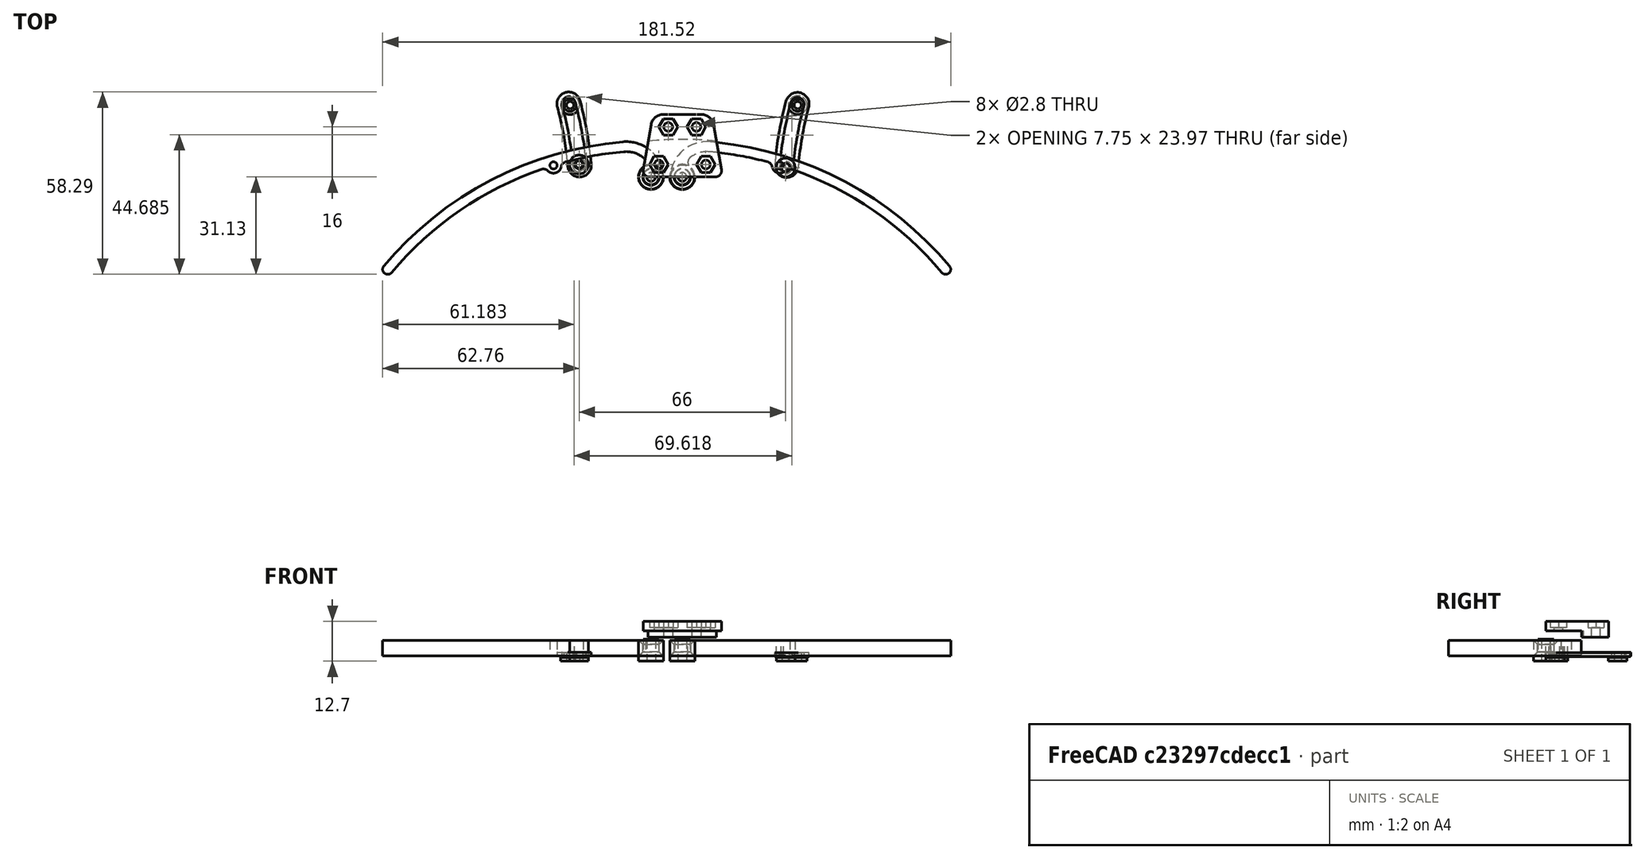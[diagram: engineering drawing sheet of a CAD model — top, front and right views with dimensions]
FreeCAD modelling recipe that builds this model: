
FCSTD DOCUMENT  (FreeCAD 0.19R24276 (Git))
Label: PB3D_TriPlate_FrontBumper
License: All rights reserved
LicenseURL: http://en.wikipedia.org/wiki/All_rights_reserved
objects: Sketcher::SketchObject×23, PartDesign::Body×13, PartDesign::Pad×7, Mesh::Feature×7, PartDesign::Revolution×6, PartDesign::Pocket×5, App::Part×5, PartDesign::Groove×2, Spreadsheet::Sheet×1, PartDesign::Plane×1
note: 77 computed .brp shape members not serialized (recipe doc carries the construction recipe); baked Part::Feature solids carry a one-line shape summary decoded from their .brp

FEATURE [Spreadsheet::Sheet] Spreadsheet  label="params"
  cells = A2=M2 Bolt Clearances; C2=M2.5 Bolt Clearances; A3=Hole Clear Diam; B3(m2_hole_clear_diam)==2.3mm; C3=Hole Clear Diam; D3(m25_hole_clear_diam)==2.8mm; E3=Std Rad; F3(std_rad)==2mm; A4=Head Clear Diam; B4(m2_head_clear_diam)==4mm; C4=Head Clear Diam; D4(m25_head_clear_diam)==5mm; A5=Head Min Depth; B5(m2_head_min_depth)==1.3mm; C5=Head Min Depth; D5(m25_head_min_depth)==1.6mm; A6=Nut Clear Flat; B6(m2_nut_clear_flat)==4.2mm; C6=Nut Clear Flat; D6(m25_nut_clear_flat)==5.2mm; A7=Nut Min Depth; B7(m2_nut_min_depth)==1.75mm; C7=Nut Min Depth; D7(m25_nut_min_depth)==2mm; A9=Bump Whisk Dims; C9=Bump Mt Plate Dims; E9=Bump Slide Dims; G9=Bumper Slide Pin; A10=Bump Diam; B10(bump_diam)==225mm; C10=MtPlate Tot Thick; D10(mtplate_tot_thick)==5mm; E10=Slide Maj Rad; F10(slide_maj_rad)==bump_diam / 2; G10=SlidePin Stop Diam; H10(slidepin_stop_diam)==6mm; A11=Bump Width; B11(bump_width)==3.2mm; C11=MtPlate Inset Thick; D11(mtplate_inset_thick)==2mm; E11=Slide Internal Width; F11(slide_internal_width)==slidepin_pin_diam + 0.3mm; G11=SlidePin Stop Height; H11(slidepin_stop_height)==1.2mm; A12=Bump Thick; B12(bump_thick)==5mm; C12=MtPlate Front Width; D12(mtplate_front_width)==20mm; E12=Slide Hoop Width; F12(slide_hoop_width)==1.6mm; G12=SlidePin Pin Diam; H12(slidepin_pin_diam)==4mm; A13=Bump Pivot Out Diam; B13(bump_pivot_out_diam)==8mm; C13=MtPlate Front Rad; D13(mtplate_front_rad)==4mm; E13=Slide Length; F13(slide_leng)==20mm; G13=SlidePin Pin Height; H13(slidepin_pin_height)==1.5mm; A14=Bump Pivot Innner Diam; B14(bump_pivot_inn_diam)==5.3mm; C14=MtPlate Back Width; D14(mtplate_back_width)==25mm; E14=Slide Thickness; F14(slide_thickness)==1.2mm; A15=Bump Slide Mt Outer Diam; B15(bump_slidemt_out_diam)==5mm; C15=MtPlate Length; D15(mtplate_leng)==20mm; G15=PinOffset Diam; H15(pinoffset_diam)==slidepin_stop_diam; A16=Bump Pivot Offset; B16(bump_pivot_offset)==8mm; C16=MtPlate Piv Hole Width; D16(mtplate_piv_hole_width)==9mm; G16=PinOffset Height; H16(pinoffset_height)==bump_thick; C17=MtPlate Hole Space L; D17(mtplate_hole_space_leng)==12mm; A18=Bump Pivot Height Tol; B18(bump_pivot_height_tol)==0.3mm; C18=MtPlate Mt Hole Width; D18(mtplate_mt_hole_width)==15mm; A19=Bump Pivot Plate Thick; B19(bump_pivot_plate_thick)==1.6mm; C19=MtPlate Mt Hole Offset L; D19(mtplate_mt_hole_offset_leng)==4mm; C20=MtPlate Circ Inset Offset ; D20(mtplate_circ_inset_offset)==12mm; A21=Bump Sweep Ang; B21(bump_sweep_ang)=45; A22=Bump Piv Angle; B22(bump_piv_ang)=12; A24=Bump Pivot Tol; B24(bump_pivot_tol)==0.3mm
FEATURE [Sketcher::SketchObject] Sketch  label="Sketch_Main_Ext"
  FullyConstrained = true
  MapMode = 5
  Support = -> [XY_Plane003]
  expr: Constraints[44] = <<params>>.bump_piv_ang
  expr: Constraints[16] = <<params>>.bump_diam
  expr: Constraints[27] = <<params>>.bump_diam
  expr: Constraints[55] = <<params>>.std_rad
  expr: Constraints[43] = 90 - <<params>>.bump_sweep_ang
  expr: Constraints[18] = <<params>>.bump_width
  expr: Constraints[35] = <<params>>.bump_slidemt_out_diam
  expr: Constraints[13] = <<params>>.bump_pivot_offset
  expr: Constraints[15] = <<params>>.bump_pivot_out_diam
  expr: Constraints[53] = <<params>>.std_rad
  sketch-geometry (21):
    g0: ArcOfCircle CenterX=0 CenterY=0 CenterZ=0 NormalX=0 NormalY=0 NormalZ=1 AngleXU=0 Radius=4 StartAngle=3.14159 EndAngle=6.28319
    g1: LineSegment StartX=8 StartY=-100.5 StartZ=0 EndX=117.3 EndY=-100.5 EndZ=0
    g2: LineSegment StartX=8 StartY=8.80001 StartZ=0 EndX=8 EndY=12 EndZ=0
    g3: ArcOfCircle CenterX=8 CenterY=-100.5 CenterZ=0 NormalX=0 NormalY=0 NormalZ=1 AngleXU=0 Radius=109.3 StartAngle=1.39858 EndAngle=1.5708
    g4: ArcOfCircle CenterX=8 CenterY=-100.5 CenterZ=0 NormalX=0 NormalY=0 NormalZ=1 AngleXU=0 Radius=112.5 StartAngle=0.785398 EndAngle=1.5708
    g5: LineSegment StartX=8 StartY=8.80001 StartZ=0 EndX=8 EndY=0 EndZ=0
    g6: LineSegment StartX=8 StartY=-100.5 StartZ=0 EndX=8 EndY=0 EndZ=0
    g7: ArcOfCircle CenterX=8 CenterY=-100.5 CenterZ=0 NormalX=0 NormalY=0 NormalZ=1 AngleXU=0 Radius=109.3 StartAngle=0.785398 EndAngle=1.32413
    g8: LineSegment StartX=8 StartY=-100.5 StartZ=0 EndX=30.7247 EndY=6.41154 EndZ=0
    g9: LineSegment StartX=8 StartY=-100.5 StartZ=0 EndX=85.2868 EndY=-23.2132 EndZ=0
    g10: LineSegment StartX=85.2868 StartY=-23.2132 StartZ=0 EndX=87.5495 EndY=-20.9505 EndZ=0
    g11: Circle CenterX=8 CenterY=-100.5 CenterZ=0 NormalX=0 NormalY=0 NormalZ=1 AngleXU=0 Radius=112.5
    g12: Circle CenterX=8 CenterY=-100.5 CenterZ=0 NormalX=0 NormalY=0 NormalZ=1 AngleXU=0 Radius=109.3
    g13: ArcOfCircle CenterX=30.7247 CenterY=6.41154 CenterZ=0 NormalX=0 NormalY=0 NormalZ=1 AngleXU=0 Radius=2.5 StartAngle=3.41123 EndAngle=5.59466
    g14: ArcOfCircle CenterX=86.4181 CenterY=-22.0819 CenterZ=0 NormalX=0 NormalY=0 NormalZ=1 AngleXU=0 Radius=1.6 StartAngle=3.92699 EndAngle=7.06858
    g15: ArcOfCircle CenterX=8.00001 CenterY=1.03132e-07 CenterZ=0 NormalX=0 NormalY=0 NormalZ=1 AngleXU=0 Radius=12 StartAngle=1.5708 EndAngle=3.14159
    g16: ArcOfCircle CenterX=0 CenterY=0 CenterZ=0 NormalX=0 NormalY=0 NormalZ=1 AngleXU=0 Radius=4 StartAngle=0 EndAngle=0.976411
    g17: ArcOfCircle CenterX=8.00001 CenterY=1.03132e-07 CenterZ=0 NormalX=0 NormalY=0 NormalZ=1 AngleXU=0 Radius=8.80001 StartAngle=1.5708 EndAngle=2.32177
    g18: ArcOfCircle CenterX=3.36 CenterY=4.97096 CenterZ=0 NormalX=0 NormalY=0 NormalZ=1 AngleXU=0 Radius=2 StartAngle=2.32177 EndAngle=4.118
    g19: ArcOfCircle CenterX=26.3873 CenterY=5.2128 CenterZ=0 NormalX=0 NormalY=0 NormalZ=1 AngleXU=0 Radius=2 StartAngle=0.269641 EndAngle=1.39858
    g20: ArcOfCircle CenterX=34.1996 CenterY=3.55226 CenterZ=0 NormalX=0 NormalY=0 NormalZ=1 AngleXU=0 Radius=2 StartAngle=1.32413 EndAngle=2.45307
  constraints (57):
    c: Coincident(g0,g-1)
    c: PointOnObject(g0,g-1)
    c: PointOnObject(g0,g-1)
    c: Horizontal(g1)
    c: Vertical(g2)
    c: Coincident(g4,g3)
    c: Coincident(g4,g2)
    c: Coincident(g5,g3)
    c: PointOnObject(g5,g-1)
    c: Vertical(g5)
    c: Coincident(g6,g3)
    c: Coincident(g6,g5)
    c: Vertical(g6)
    c: DistanceX(g0,g5) = 8
    c: Coincident(g2,g3)
    c: Diameter(g0) = 8
    c: Diameter(g4) = 225
    c: Coincident(g1,g3)
    c: DistanceY(g3,g4) = 3.2
    c: Coincident(g7,g3)
    c: Coincident(g8,g3)
    c: Coincident(g9,g3)
    c: Coincident(g9,g7)
    c: Coincident(g10,g7)
    c: Coincident(g10,g4)
    c: Parallel(g9,g10)
    c: Coincident(g11,g3)
    c: Diameter(g11) = 225
    c: Coincident(g12,g3)
    c: PointOnObject(g3,g12)
    c: PointOnObject(g13,g12)
    c: Coincident(g8,g13)
    c: PointOnObject(g14,g10)
    c: Coincident(g14,g7)
    c: Coincident(g14,g4)
    c: Diameter(g13) = 5
    c: Coincident(g15,g4)
    c: Coincident(g15,g0)
    c: Coincident(g16,g0)
    c: Coincident(g17,g15)
    c: Coincident(g17,g3)
    c: Coincident(g16,g0)
    c: PointOnObject(g1,g12)
    c: Angle(g1,g9) = 0.785398
    c: Angle(g8,g6) = 0.20944
    c: Tangent(g0,g15)
    c: Tangent(g15,g4)
    c: Tangent(g16,g18) = 1.5708
    c: Tangent(g17,g18) = -1.5708
    c: Tangent(g13,g19) = 1.5708
    c: Tangent(g3,g19) = -1.5708
    c: Tangent(g13,g20) = 1.5708
    c: Tangent(g7,g20) = -1.5708
    c: Radius(g18) = 2
    c: Equal(g19,g20)
    c: Radius(g20) = 2
    c: PointOnObject(g7,g12)
FEATURE [PartDesign::Pad] Pad  label="MainExt"
  Direction = (1,1,1)
  Length = 5
  Length2 = 100
  Profile = -> Sketch
  Reversed = true
  Type = 0
  expr: Length = <<params>>.bump_thick
FEATURE [Sketcher::SketchObject] Sketch001  label="Sketch_Main_Ext_Temp"
  FullyConstrained = true
  MapMode = 5
  Support = -> [XY_Plane003]
  expr: Constraints[53] = <<params>>.std_rad
  expr: Constraints[15] = <<params>>.bump_pivot_out_diam
  expr: Constraints[13] = <<params>>.bump_pivot_offset
  expr: Constraints[35] = <<params>>.bump_slidemt_out_diam
  expr: Constraints[18] = <<params>>.bump_width
  expr: Constraints[55] = <<params>>.std_rad
  expr: Constraints[27] = <<params>>.bump_diam
  expr: Constraints[16] = <<params>>.bump_diam
  sketch-geometry (21):
    g0: ArcOfCircle CenterX=0 CenterY=0 CenterZ=0 NormalX=0 NormalY=0 NormalZ=1 AngleXU=0 Radius=4 StartAngle=3.14159 EndAngle=6.28319
    g1: LineSegment StartX=8 StartY=-100.5 StartZ=0 EndX=117.3 EndY=-100.5 EndZ=0
    g2: LineSegment StartX=8 StartY=8.79997 StartZ=0 EndX=8 EndY=12 EndZ=0
    g3: ArcOfCircle CenterX=8 CenterY=-100.5 CenterZ=0 NormalX=0 NormalY=0 NormalZ=1 AngleXU=0 Radius=109.3 StartAngle=1.34622 EndAngle=1.5708
    g4: ArcOfCircle CenterX=8 CenterY=-100.5 CenterZ=0 NormalX=0 NormalY=0 NormalZ=1 AngleXU=0 Radius=112.5 StartAngle=0.349066 EndAngle=1.5708
    g5: LineSegment StartX=8 StartY=8.79997 StartZ=0 EndX=8 EndY=0 EndZ=0
    g6: LineSegment StartX=8 StartY=-100.5 StartZ=0 EndX=8 EndY=0 EndZ=0
    g7: ArcOfCircle CenterX=8 CenterY=-100.5 CenterZ=0 NormalX=0 NormalY=0 NormalZ=1 AngleXU=0 Radius=109.3 StartAngle=0.349066 EndAngle=1.27177
    g8: LineSegment StartX=8 StartY=-100.5 StartZ=0 EndX=36.2889 EndY=5.07567 EndZ=0
    g9: LineSegment StartX=8 StartY=-100.5 StartZ=0 EndX=110.708 EndY=-63.1172 EndZ=0
    g10: LineSegment StartX=110.708 StartY=-63.1172 StartZ=0 EndX=113.715 EndY=-62.0228 EndZ=0
    g11: Circle CenterX=8 CenterY=-100.5 CenterZ=0 NormalX=0 NormalY=0 NormalZ=1 AngleXU=0 Radius=112.5
    g12: Circle CenterX=8 CenterY=-100.5 CenterZ=0 NormalX=0 NormalY=0 NormalZ=1 AngleXU=0 Radius=109.3
    g13: ArcOfCircle CenterX=36.2889 CenterY=5.07567 CenterZ=0 NormalX=0 NormalY=0 NormalZ=1 AngleXU=0 Radius=2.5 StartAngle=3.35887 EndAngle=5.54231
    g14: ArcOfCircle CenterX=112.212 CenterY=-62.57 CenterZ=0 NormalX=0 NormalY=0 NormalZ=1 AngleXU=0 Radius=1.6 StartAngle=3.49066 EndAngle=6.63225
    g15: ArcOfCircle CenterX=7.99997 CenterY=1.02572e-07 CenterZ=0 NormalX=0 NormalY=0 NormalZ=1 AngleXU=0 Radius=12 StartAngle=1.57079 EndAngle=3.14159
    g16: ArcOfCircle CenterX=0 CenterY=0 CenterZ=0 NormalX=0 NormalY=0 NormalZ=1 AngleXU=0 Radius=4 StartAngle=0 EndAngle=0.976409
    g17: ArcOfCircle CenterX=7.99997 CenterY=1.02572e-07 CenterZ=0 NormalX=0 NormalY=0 NormalZ=1 AngleXU=0 Radius=8.79997 StartAngle=1.57079 EndAngle=2.32177
    g18: ArcOfCircle CenterX=3.36001 CenterY=4.97095 CenterZ=0 NormalX=0 NormalY=0 NormalZ=1 AngleXU=0 Radius=2 StartAngle=2.32177 EndAngle=4.118
    g19: ArcOfCircle CenterX=31.8947 CenterY=4.10558 CenterZ=0 NormalX=0 NormalY=0 NormalZ=1 AngleXU=0 Radius=2 StartAngle=0.217281 EndAngle=1.34622
    g20: ArcOfCircle CenterX=39.6094 CenterY=2.03845 CenterZ=0 NormalX=0 NormalY=0 NormalZ=1 AngleXU=0 Radius=2 StartAngle=1.27177 EndAngle=2.40071
  constraints (57):
    c: Coincident(g0,g-1)
    c: PointOnObject(g0,g-1)
    c: PointOnObject(g0,g-1)
    c: Horizontal(g1)
    c: Vertical(g2)
    c: Coincident(g4,g3)
    c: Coincident(g4,g2)
    c: Coincident(g5,g3)
    c: PointOnObject(g5,g-1)
    c: Vertical(g5)
    c: Coincident(g6,g3)
    c: Coincident(g6,g5)
    c: Vertical(g6)
    c: DistanceX(g0,g5) = 8
    c: Coincident(g2,g3)
    c: Diameter(g0) = 8
    c: Diameter(g4) = 225
    c: Coincident(g1,g3)
    c: DistanceY(g3,g4) = 3.2
    c: Coincident(g7,g3)
    c: Coincident(g8,g3)
    c: Coincident(g9,g3)
    c: Coincident(g9,g7)
    c: Coincident(g10,g7)
    c: Coincident(g10,g4)
    c: Parallel(g9,g10)
    c: Coincident(g11,g3)
    c: Diameter(g11) = 225
    c: Coincident(g12,g3)
    c: PointOnObject(g3,g12)
    c: PointOnObject(g13,g12)
    c: Coincident(g8,g13)
    c: PointOnObject(g14,g10)
    c: Coincident(g14,g7)
    c: Coincident(g14,g4)
    c: Diameter(g13) = 5
    c: Coincident(g15,g4)
    c: Coincident(g15,g0)
    c: Coincident(g16,g0)
    c: Coincident(g17,g15)
    c: Coincident(g17,g3)
    c: Coincident(g16,g0)
    c: PointOnObject(g1,g12)
    c: Angle(g1,g9) = 0.349066
    c: Angle(g8,g6) = 0.261799
    c: Tangent(g0,g15)
    c: Tangent(g15,g4)
    c: Tangent(g16,g18) = 1.5708
    c: Tangent(g17,g18) = -1.5708
    c: Tangent(g13,g19) = 1.5708
    c: Tangent(g3,g19) = -1.5708
    c: Tangent(g13,g20) = 1.5708
    c: Tangent(g7,g20) = -1.5708
    c: Radius(g18) = 2
    c: Equal(g19,g20)
    c: Radius(g20) = 2
    c: PointOnObject(g7,g12)
FEATURE [Sketcher::SketchObject] Sketch002  label="Sketch_SlideHole"
  FullyConstrained = true
  MapMode = 5
  Support = -> [XY_Plane003]
  expr: Constraints[44] = <<params>>.bump_piv_ang
  expr: Constraints[16] = <<params>>.bump_diam
  expr: Constraints[27] = <<params>>.bump_diam
  expr: Constraints[55] = <<params>>.std_rad
  expr: Constraints[18] = <<params>>.bump_width
  expr: Constraints[35] = <<params>>.bump_slidemt_out_diam
  expr: Constraints[13] = <<params>>.bump_pivot_offset
  expr: Constraints[53] = <<params>>.std_rad
  expr: Constraints[15] = <<params>>.bump_pivot_out_diam
  expr: Constraints[58] = <<params>>.m2_hole_clear_diam
  sketch-geometry (22):
    g0: ArcOfCircle CenterX=0 CenterY=0 CenterZ=0 NormalX=0 NormalY=0 NormalZ=1 AngleXU=0 Radius=4 StartAngle=3.14159 EndAngle=6.28319
    g1: LineSegment StartX=8 StartY=-100.5 StartZ=0 EndX=117.3 EndY=-100.5 EndZ=0
    g2: LineSegment StartX=8 StartY=8.8 StartZ=0 EndX=8 EndY=12 EndZ=0
    g3: ArcOfCircle CenterX=8 CenterY=-100.5 CenterZ=0 NormalX=0 NormalY=0 NormalZ=1 AngleXU=0 Radius=109.3 StartAngle=1.39858 EndAngle=1.5708
    g4: ArcOfCircle CenterX=8 CenterY=-100.5 CenterZ=0 NormalX=0 NormalY=0 NormalZ=1 AngleXU=0 Radius=112.5 StartAngle=0.349066 EndAngle=1.5708
    g5: LineSegment StartX=8 StartY=8.8 StartZ=0 EndX=8 EndY=0 EndZ=0
    g6: LineSegment StartX=8 StartY=-100.5 StartZ=0 EndX=8 EndY=0 EndZ=0
    g7: ArcOfCircle CenterX=8 CenterY=-100.5 CenterZ=0 NormalX=0 NormalY=0 NormalZ=1 AngleXU=0 Radius=109.3 StartAngle=0.349066 EndAngle=1.32413
    g8: LineSegment StartX=8 StartY=-100.5 StartZ=0 EndX=30.7247 EndY=6.41154 EndZ=0
    g9: LineSegment StartX=8 StartY=-100.5 StartZ=0 EndX=110.708 EndY=-63.1172 EndZ=0
    g10: LineSegment StartX=110.708 StartY=-63.1172 StartZ=0 EndX=113.715 EndY=-62.0227 EndZ=0
    g11: Circle CenterX=8 CenterY=-100.5 CenterZ=0 NormalX=0 NormalY=0 NormalZ=1 AngleXU=0 Radius=112.5
    g12: Circle CenterX=8 CenterY=-100.5 CenterZ=0 NormalX=0 NormalY=0 NormalZ=1 AngleXU=0 Radius=109.3
    g13: ArcOfCircle CenterX=30.7247 CenterY=6.41154 CenterZ=0 NormalX=0 NormalY=0 NormalZ=1 AngleXU=0 Radius=2.5 StartAngle=3.41123 EndAngle=5.59466
    g14: ArcOfCircle CenterX=112.212 CenterY=-62.57 CenterZ=0 NormalX=0 NormalY=0 NormalZ=1 AngleXU=0 Radius=1.6 StartAngle=3.49066 EndAngle=6.63225
    g15: ArcOfCircle CenterX=8 CenterY=3.30857e-07 CenterZ=0 NormalX=0 NormalY=0 NormalZ=1 AngleXU=0 Radius=12 StartAngle=1.5708 EndAngle=3.14159
    g16: ArcOfCircle CenterX=0 CenterY=0 CenterZ=0 NormalX=0 NormalY=0 NormalZ=1 AngleXU=0 Radius=4 StartAngle=0 EndAngle=0.976411
    g17: ArcOfCircle CenterX=8 CenterY=3.30857e-07 CenterZ=0 NormalX=0 NormalY=0 NormalZ=1 AngleXU=0 Radius=8.8 StartAngle=1.5708 EndAngle=2.32177
    g18: ArcOfCircle CenterX=3.36 CenterY=4.97096 CenterZ=0 NormalX=0 NormalY=0 NormalZ=1 AngleXU=0 Radius=2 StartAngle=2.32177 EndAngle=4.118
    g19: ArcOfCircle CenterX=26.3873 CenterY=5.2128 CenterZ=0 NormalX=0 NormalY=0 NormalZ=1 AngleXU=0 Radius=2 StartAngle=0.269641 EndAngle=1.39858
    g20: ArcOfCircle CenterX=34.1996 CenterY=3.55226 CenterZ=0 NormalX=0 NormalY=0 NormalZ=1 AngleXU=0 Radius=2 StartAngle=1.32413 EndAngle=2.45307
    g21: Circle CenterX=30.7247 CenterY=6.41154 CenterZ=0 NormalX=0 NormalY=0 NormalZ=1 AngleXU=0 Radius=1.15
  constraints (59):
    c: Coincident(g0,g-1)
    c: PointOnObject(g0,g-1)
    c: PointOnObject(g0,g-1)
    c: Horizontal(g1)
    c: Vertical(g2)
    c: Coincident(g4,g3)
    c: Coincident(g4,g2)
    c: Coincident(g5,g3)
    c: PointOnObject(g5,g-1)
    c: Vertical(g5)
    c: Coincident(g6,g3)
    c: Coincident(g6,g5)
    c: Vertical(g6)
    c: DistanceX(g0,g5) = 8
    c: Coincident(g2,g3)
    c: Diameter(g0) = 8
    c: Diameter(g4) = 225
    c: Coincident(g1,g3)
    c: DistanceY(g3,g4) = 3.2
    c: Coincident(g7,g3)
    c: Coincident(g8,g3)
    c: Coincident(g9,g3)
    c: Coincident(g9,g7)
    c: Coincident(g10,g7)
    c: Coincident(g10,g4)
    c: Parallel(g9,g10)
    c: Coincident(g11,g3)
    c: Diameter(g11) = 225
    c: Coincident(g12,g3)
    c: PointOnObject(g3,g12)
    c: PointOnObject(g13,g12)
    c: Coincident(g8,g13)
    c: PointOnObject(g14,g10)
    c: Coincident(g14,g7)
    c: Coincident(g14,g4)
    c: Diameter(g13) = 5
    c: Coincident(g15,g4)
    c: Coincident(g15,g0)
    c: Coincident(g16,g0)
    c: Coincident(g17,g15)
    c: Coincident(g17,g3)
    c: Coincident(g16,g0)
    c: PointOnObject(g1,g12)
    c: Angle(g1,g9) = 0.349066
    c: Angle(g8,g6) = 0.20944
    c: Tangent(g0,g15)
    c: Tangent(g15,g4)
    c: Tangent(g16,g18) = 1.5708
    c: Tangent(g17,g18) = -1.5708
    c: Tangent(g13,g19) = 1.5708
    c: Tangent(g3,g19) = -1.5708
    c: Tangent(g13,g20) = 1.5708
    c: Tangent(g7,g20) = -1.5708
    c: Radius(g18) = 2
    c: Equal(g19,g20)
    c: Radius(g20) = 2
    c: PointOnObject(g7,g12)
    c: Coincident(g21,g8)
    c: Diameter(g21) = 2.3
FEATURE [PartDesign::Pocket] Pocket  label="SlideMtHole"
  BaseFeature = -> Pad
  Length = 5
  Length2 = 100
  Midplane = true
  Profile = -> Sketch002
  Type = 1
FEATURE [Sketcher::SketchObject] Sketch003
  FullyConstrained = true
  MapMode = 5
  Placement = pos=(0,0,0) rot=(1,0,0;1.5708rad)
  Support = -> [XZ_Plane003]
  expr: Constraints[16] = <<params>>.bump_pivot_inn_diam / 2
  expr: Constraints[17] = <<params>>.bump_thick
  expr: Constraints[18] = <<params>>.bump_thick / 4
  sketch-geometry (7):
    g0: LineSegment StartX=0 StartY=0 StartZ=0 EndX=3.9 EndY=0 EndZ=0
    g1: LineSegment StartX=3.9 StartY=0 StartZ=0 EndX=2.65 EndY=-1.25 EndZ=0
    g2: LineSegment StartX=2.65 StartY=-1.25 StartZ=0 EndX=2.65 EndY=-3.75 EndZ=0
    g3: LineSegment StartX=2.65 StartY=-3.75 StartZ=0 EndX=3.9 EndY=-5 EndZ=0
    g4: LineSegment StartX=3.9 StartY=-5 StartZ=0 EndX=0 EndY=-5 EndZ=0
    g5: LineSegment StartX=0 StartY=-5 StartZ=0 EndX=0 EndY=0 EndZ=0
    g6: LineSegment StartX=3.9 StartY=0 StartZ=0 EndX=3.9 EndY=-5 EndZ=0
  constraints (19):
    c: Coincident(g0,g-1)
    c: PointOnObject(g0,g-1)
    c: Coincident(g1,g0)
    c: Coincident(g2,g1)
    c: Vertical(g2)
    c: Coincident(g3,g2)
    c: Coincident(g4,g3)
    c: PointOnObject(g4,g-2)
    c: Coincident(g5,g4)
    c: Coincident(g5,g0)
    c: Horizontal(g4)
    c: Coincident(g6,g0)
    c: Coincident(g6,g3)
    c: Vertical(g6)
    c: Angle(g0,g1) = 0.785398
    c: Angle(g3,g4) = 0.785398
    c: DistanceX(g4,g2) = 2.65
    c: DistanceY(g4,g0) = 5
    c: DistanceY(g1,g0) = 1.25
FEATURE [PartDesign::Groove] Groove
  Angle = 360
  Axis = (0,-2e-16,1)
  Base = (0,0,0)
  BaseFeature = -> Pocket
  Profile = -> Sketch003
  ReferenceAxis = -> Sketch003 [V_Axis]
FEATURE [PartDesign::Body] Body001  label="BumpWhisker"
  Group = -> [Sketch,Pad,Sketch001,Sketch002,Pocket,Sketch003,Groove]
  Origin = -> Origin003
  Placement = pos=(0,0,-6) rot=(0,0,-1;0.087266rad)
  Tip = -> Groove
FEATURE [Sketcher::SketchObject] Sketch004
  FullyConstrained = true
  MapMode = 5
  Placement = pos=(0,0,0) rot=(1,0,0;1.5708rad)
  Support = -> [XZ_Plane010]
  expr: Constraints[15] = <<params>>.bump_thick / 4
  expr: Constraints[20] = <<params>>.bump_pivot_out_diam / 2
  expr: Constraints[16] = <<params>>.bump_thick
  expr: Constraints[13] = <<params>>.bump_pivot_plate_thick
  expr: Constraints[14] = <<params>>.bump_pivot_height_tol
  expr: Constraints[22] = <<params>>.m25_hole_clear_diam / 2
  expr: Constraints[21] = (<<params>>.bump_pivot_inn_diam - <<params>>.bump_pivot_tol) / 2
  sketch-geometry (8):
    g0: LineSegment StartX=1.4 StartY=0.3 StartZ=0 EndX=2.5 EndY=0.3 EndZ=0
    g1: LineSegment StartX=2.5 StartY=0.3 StartZ=0 EndX=2.5 EndY=-3.75 EndZ=0
    g2: LineSegment StartX=2.5 StartY=-3.75 StartZ=0 EndX=3.75 EndY=-5 EndZ=0
    g3: LineSegment StartX=3.75 StartY=-5 StartZ=0 EndX=4 EndY=-5 EndZ=0
    g4: LineSegment StartX=4 StartY=-5 StartZ=0 EndX=4 EndY=-6.6 EndZ=0
    g5: LineSegment StartX=4 StartY=-6.6 StartZ=0 EndX=1.4 EndY=-6.6 EndZ=0
    g6: LineSegment StartX=3.75 StartY=-5 StartZ=0 EndX=0 EndY=-5 EndZ=0
    g7: LineSegment StartX=1.4 StartY=0.3 StartZ=0 EndX=1.4 EndY=-6.6 EndZ=0
  constraints (24):
    c: Horizontal(g0)
    c: Coincident(g1,g0)
    c: Vertical(g1)
    c: Coincident(g2,g1)
    c: Coincident(g3,g2)
    c: Horizontal(g3)
    c: Coincident(g4,g3)
    c: Vertical(g4)
    c: Coincident(g5,g4)
    c: Horizontal(g5)
    c: Coincident(g6,g2)
    c: Horizontal(g6)
    c: Angle(g2,g6) = 0.785398
    c: DistanceY(g4,g3) = 1.6
    c: DistanceY(g-1,g0) = 0.3
    c: DistanceY(g2,g1) = 1.25
    c: DistanceY(g2,g-1) = 5
    c: Coincident(g7,g0)
    c: Coincident(g7,g5)
    c: Vertical(g7)
    c: DistanceX(g-1,g4) = 4
    c: DistanceX(g-1,g0) = 2.5
    c: DistanceX(g-1,g0) = 1.4
    c: PointOnObject(g6,g-2)
FEATURE [PartDesign::Revolution] Revolution
  Angle = 360
  Axis = (0,-2e-16,1)
  Base = (0,0,0)
  Placement = pos=(0,0,0) rot=(1,0,0;1.5708rad)
  Profile = -> Sketch004
  ReferenceAxis = -> Sketch004 [V_Axis]
  Reversed = true
FEATURE [PartDesign::Body] Body005  label="BumpPivot"
  Group = -> [Sketch004,Revolution]
  Origin = -> Origin010
  Placement = pos=(0,0,-6) rot=(0,0,1;0rad)
  Tip = -> Revolution
FEATURE [Sketcher::SketchObject] Sketch005  label="Sketch_MainPlate"
  FullyConstrained = true
  MapMode = 5
  Support = -> [XY_Plane001]
  expr: Constraints[20] = <<params>>.mtplate_leng
  expr: Constraints[18] = <<params>>.mtplate_front_width
  expr: Constraints[21] = <<params>>.bump_pivot_out_diam / 2
  expr: Constraints[19] = <<params>>.mtplate_back_width
  expr: Constraints[23] = <<params>>.std_rad
  sketch-geometry (10):
    g0: LineSegment StartX=-10.5297 StartY=0 StartZ=0 EndX=10.5297 EndY=0 EndZ=0
    g1: LineSegment StartX=-12.5 StartY=2.34341 StartZ=0 EndX=-10 EndY=16.6868 EndZ=0
    g2: LineSegment StartX=-6.05941 StartY=20 StartZ=0 EndX=6.05941 EndY=20 EndZ=0
    g3: LineSegment StartX=10 StartY=16.6868 StartZ=0 EndX=12.5 EndY=2.34341 EndZ=0
    g4: LineSegment StartX=0 StartY=0 StartZ=0 EndX=0 EndY=20 EndZ=0
    g5: LineSegment StartX=0 StartY=0 StartZ=0 EndX=2e-16 EndY=0 EndZ=0
    g6: ArcOfCircle CenterX=-6.05941 CenterY=16 CenterZ=0 NormalX=0 NormalY=0 NormalZ=1 AngleXU=0 Radius=4 StartAngle=1.5708 EndAngle=2.96903
    g7: ArcOfCircle CenterX=6.05941 CenterY=16 CenterZ=0 NormalX=0 NormalY=0 NormalZ=1 AngleXU=0 Radius=4 StartAngle=0.172563 EndAngle=1.5708
    g8: ArcOfCircle CenterX=-10.5297 CenterY=2 CenterZ=0 NormalX=0 NormalY=0 NormalZ=1 AngleXU=0 Radius=2 StartAngle=2.96903 EndAngle=4.71239
    g9: ArcOfCircle CenterX=10.5297 CenterY=2 CenterZ=0 NormalX=0 NormalY=0 NormalZ=1 AngleXU=0 Radius=2 StartAngle=4.71239 EndAngle=6.45575
  constraints (24):
    c: Horizontal(g0)
    c: Horizontal(g2)
    c: Coincident(g4,g-1)
    c: PointOnObject(g4,g-2)
    c: Coincident(g5,g-1)
    c: PointOnObject(g5,g-2)
    c: Tangent(g1,g6) = 1.5708
    c: Tangent(g2,g6) = 1.5708
    c: Tangent(g2,g7) = 1.5708
    c: Tangent(g3,g7) = 1.5708
    c: Tangent(g1,g8) = 1.5708
    c: Tangent(g0,g8) = -1.5708
    c: Tangent(g0,g9) = -1.5708
    c: Tangent(g3,g9) = 1.5708
    c: Equal(g9,g8)
    c: Equal(g6,g7)
    c: Symmetric(g2,g2,g4)
    c: Symmetric(g0,g0,g5)
    c: DistanceX(g1,g3) = 20
    c: DistanceX(g1,g3) = 25
    c: DistanceY(g0,g2) = 20
    c: Radius(g7) = 4
    c: PointOnObject(g0,g-1)
    c: Radius(g9) = 2
FEATURE [PartDesign::Pad] Pad001  label="MainPlateExt"
  Direction = (1,1,1)
  Length = 5
  Length2 = 100
  Profile = -> Sketch005
  Reversed = true
  Type = 0
  expr: Length = <<params>>.mtplate_tot_thick
FEATURE [PartDesign::Plane] DatumPlane  label="Datum_InsetLocZ"
  AttachmentOffset = pos=(0,0,-3) rot=(0,0,1;0rad)
  Length = 60
  MapMode = 5
  Placement = pos=(0,0,-3) rot=(0,0,1;0rad)
  ResizeMode = 0
  Support = -> [XY_Plane001]
  Width = 60
  expr: .AttachmentOffset.Base.z = -1 * (<<params>>.mtplate_tot_thick - <<params>>.mtplate_inset_thick)
FEATURE [Sketcher::SketchObject] Sketch006  label="Sketch_PivNMtHoles_Temp"
  FullyConstrained = true
  MapMode = 5
  Support = -> [XY_Plane001]
  expr: Constraints[11] = <<params>>.mtplate_piv_hole_width
  expr: Constraints[10] = <<params>>.mtplate_mt_hole_width
  expr: Constraints[9] = <<params>>.mtplate_hole_space_leng
  expr: Constraints[8] = <<params>>.mtplate_mt_hole_offset_leng
  sketch-geometry (4):
    g0: LineSegment StartX=-7.5 StartY=4 StartZ=0 EndX=7.5 EndY=4 EndZ=0
    g1: LineSegment StartX=0 StartY=0 StartZ=0 EndX=0 EndY=4 EndZ=0
    g2: LineSegment StartX=0 StartY=0 StartZ=0 EndX=0 EndY=16 EndZ=0
    g3: LineSegment StartX=-4.5 StartY=16 StartZ=0 EndX=4.5 EndY=16 EndZ=0
  constraints (12):
    c: Horizontal(g0)
    c: Coincident(g1,g-1)
    c: PointOnObject(g1,g-2)
    c: Coincident(g2,g-1)
    c: PointOnObject(g2,g-2)
    c: Horizontal(g3)
    c: Symmetric(g3,g3,g2)
    c: Symmetric(g0,g0,g1)
    c: DistanceY(g-1,g1) = 4
    c: DistanceY(g1,g2) = 12
    c: DistanceX(g0,g0) = 15
    c: DistanceX(g3,g3) = 9
FEATURE [Sketcher::SketchObject] Sketch007  label="Sketch_PivNMtHoles"
  FullyConstrained = true
  MapMode = 5
  Support = -> [XY_Plane001]
  expr: Constraints[19] = <<params>>.m25_hole_clear_diam
  expr: Constraints[8] = <<params>>.mtplate_mt_hole_offset_leng
  expr: Constraints[9] = <<params>>.mtplate_hole_space_leng
  expr: Constraints[10] = <<params>>.mtplate_mt_hole_width
  expr: Constraints[11] = <<params>>.mtplate_piv_hole_width
  sketch-geometry (8):
    g0: LineSegment StartX=-7.5 StartY=4 StartZ=0 EndX=7.5 EndY=4 EndZ=0
    g1: LineSegment StartX=0 StartY=0 StartZ=0 EndX=0 EndY=4 EndZ=0
    g2: LineSegment StartX=0 StartY=0 StartZ=0 EndX=0 EndY=16 EndZ=0
    g3: LineSegment StartX=-4.5 StartY=16 StartZ=0 EndX=4.5 EndY=16 EndZ=0
    g4: Circle CenterX=-4.5 CenterY=16 CenterZ=0 NormalX=0 NormalY=0 NormalZ=1 AngleXU=0 Radius=1.4
    g5: Circle CenterX=4.5 CenterY=16 CenterZ=0 NormalX=0 NormalY=0 NormalZ=1 AngleXU=0 Radius=1.4
    g6: Circle CenterX=7.5 CenterY=4 CenterZ=0 NormalX=0 NormalY=0 NormalZ=1 AngleXU=0 Radius=1.4
    g7: Circle CenterX=-7.5 CenterY=4 CenterZ=0 NormalX=0 NormalY=0 NormalZ=1 AngleXU=0 Radius=1.4
  constraints (20):
    c: Horizontal(g0)
    c: Coincident(g1,g-1)
    c: PointOnObject(g1,g-2)
    c: Coincident(g2,g-1)
    c: PointOnObject(g2,g-2)
    c: Horizontal(g3)
    c: Symmetric(g3,g3,g2)
    c: Symmetric(g0,g0,g1)
    c: DistanceY(g-1,g1) = 4
    c: DistanceY(g1,g2) = 12
    c: DistanceX(g0,g0) = 15
    c: DistanceX(g3,g3) = 9
    c: Coincident(g4,g3)
    c: Coincident(g5,g3)
    c: Coincident(g6,g0)
    c: Coincident(g7,g0)
    c: Equal(g6,g7)
    c: Equal(g7,g4)
    c: Equal(g4,g5)
    c: Diameter(g6) = 2.8
FEATURE [PartDesign::Pocket] Pocket001  label="PivNMtHoles"
  BaseFeature = -> Pad001
  Length = 5
  Length2 = 100
  Midplane = true
  Profile = -> Sketch007
  Type = 1
FEATURE [Sketcher::SketchObject] Sketch008  label="Sketch_PivNMtHexSunk"
  FullyConstrained = true
  MapMode = 5
  Support = -> [XY_Plane001]
  expr: Constraints[8] = <<params>>.mtplate_mt_hole_offset_leng
  expr: Constraints[9] = <<params>>.mtplate_hole_space_leng
  expr: Constraints[91] = <<params>>.m25_nut_clear_flat
  expr: Constraints[10] = <<params>>.mtplate_mt_hole_width
  expr: Constraints[11] = <<params>>.mtplate_piv_hole_width
  sketch-geometry (32):
    g0: LineSegment StartX=-7.5 StartY=4 StartZ=0 EndX=7.5 EndY=4 EndZ=0
    g1: LineSegment StartX=0 StartY=0 StartZ=0 EndX=0 EndY=4 EndZ=0
    g2: LineSegment StartX=0 StartY=0 StartZ=0 EndX=0 EndY=16 EndZ=0
    g3: LineSegment StartX=-4.5 StartY=16 StartZ=0 EndX=4.5 EndY=16 EndZ=0
    g4: LineSegment StartX=-9.00111 StartY=6.6 StartZ=0 EndX=-10.5022 EndY=4 EndZ=0
    g5: LineSegment StartX=-10.5022 StartY=4 StartZ=0 EndX=-9.00111 EndY=1.4 EndZ=0
    g6: LineSegment StartX=-9.00111 StartY=1.4 StartZ=0 EndX=-5.99889 EndY=1.4 EndZ=0
    g7: LineSegment StartX=-5.99889 StartY=1.4 StartZ=0 EndX=-4.49778 EndY=4 EndZ=0
    g8: LineSegment StartX=-4.49778 StartY=4 StartZ=0 EndX=-5.99889 EndY=6.6 EndZ=0
    g9: LineSegment StartX=-5.99889 StartY=6.6 StartZ=0 EndX=-9.00111 EndY=6.6 EndZ=0
    g10: Circle CenterX=-7.5 CenterY=4 CenterZ=0 NormalX=0 NormalY=0 NormalZ=1 AngleXU=0 Radius=3.00222
    g11: LineSegment StartX=9.00111 StartY=1.4 StartZ=0 EndX=10.5022 EndY=4 EndZ=0
    g12: LineSegment StartX=10.5022 StartY=4 StartZ=0 EndX=9.00111 EndY=6.6 EndZ=0
    g13: LineSegment StartX=9.00111 StartY=6.6 StartZ=0 EndX=5.99889 EndY=6.6 EndZ=0
    g14: LineSegment StartX=5.99889 StartY=6.6 StartZ=0 EndX=4.49778 EndY=4 EndZ=0
    g15: LineSegment StartX=4.49778 StartY=4 StartZ=0 EndX=5.99889 EndY=1.4 EndZ=0
    g16: LineSegment StartX=5.99889 StartY=1.4 StartZ=0 EndX=9.00111 EndY=1.4 EndZ=0
    g17: Circle CenterX=7.5 CenterY=4 CenterZ=0 NormalX=0 NormalY=0 NormalZ=1 AngleXU=0 Radius=3.00222
    g18: LineSegment StartX=6.00111 StartY=13.4 StartZ=0 EndX=7.50222 EndY=16 EndZ=0
    g19: LineSegment StartX=7.50222 StartY=16 StartZ=0 EndX=6.00111 EndY=18.6 EndZ=0
    g20: LineSegment StartX=6.00111 StartY=18.6 StartZ=0 EndX=2.99889 EndY=18.6 EndZ=0
    g21: LineSegment StartX=2.99889 StartY=18.6 StartZ=0 EndX=1.49778 EndY=16 EndZ=0
    g22: LineSegment StartX=1.49778 StartY=16 StartZ=0 EndX=2.99889 EndY=13.4 EndZ=0
    g23: LineSegment StartX=2.99889 StartY=13.4 StartZ=0 EndX=6.00111 EndY=13.4 EndZ=0
    g24: Circle CenterX=4.5 CenterY=16 CenterZ=0 NormalX=0 NormalY=0 NormalZ=1 AngleXU=0 Radius=3.00222
    g25: LineSegment StartX=-6.00111 StartY=13.4 StartZ=0 EndX=-2.99889 EndY=13.4 EndZ=0
    g26: LineSegment StartX=-2.99889 StartY=13.4 StartZ=0 EndX=-1.49778 EndY=16 EndZ=0
    g27: LineSegment StartX=-1.49778 StartY=16 StartZ=0 EndX=-2.99889 EndY=18.6 EndZ=0
    g28: LineSegment StartX=-2.99889 StartY=18.6 StartZ=0 EndX=-6.00111 EndY=18.6 EndZ=0
    g29: LineSegment StartX=-6.00111 StartY=18.6 StartZ=0 EndX=-7.50222 EndY=16 EndZ=0
    g30: LineSegment StartX=-7.50222 StartY=16 StartZ=0 EndX=-6.00111 EndY=13.4 EndZ=0
    g31: Circle CenterX=-4.5 CenterY=16 CenterZ=0 NormalX=0 NormalY=0 NormalZ=1 AngleXU=0 Radius=3.00222
  constraints (76):
    c: Horizontal(g0)
    c: Coincident(g1,g-1)
    c: PointOnObject(g1,g-2)
    c: Coincident(g2,g-1)
    c: PointOnObject(g2,g-2)
    c: Horizontal(g3)
    c: Symmetric(g3,g3,g2)
    c: Symmetric(g0,g0,g1)
    c: DistanceY(g-1,g1) = 4
    c: DistanceY(g1,g2) = 12
    c: DistanceX(g0,g0) = 15
    c: DistanceX(g3,g3) = 9
    c: Coincident(g4,g5)
    c: Coincident(g5,g6)
    c: Coincident(g6,g7)
    c: Coincident(g7,g8)
    c: Coincident(g8,g9)
    c: Coincident(g9,g4)
    c: Equal(g4, g5-g9) x5
    c: PointOnObject(g4,g10)
    c: PointOnObject(g5,g10)
    c: PointOnObject(g6,g10)
    c: PointOnObject(g7,g10)
    c: PointOnObject(g8,g10)
    c: PointOnObject(g9,g10)
    c: Coincident(g10,g0)
    c: Coincident(g11,g12)
    c: Coincident(g12,g13)
    c: Coincident(g13,g14)
    c: Coincident(g14,g15)
    c: Coincident(g15,g16)
    c: Coincident(g16,g11)
    c: Equal(g11, g12-g16) x5
    c: PointOnObject(g11,g17)
    c: PointOnObject(g12,g17)
    c: PointOnObject(g13,g17)
    c: PointOnObject(g14,g17)
    c: PointOnObject(g15,g17)
    c: PointOnObject(g16,g17)
    c: Coincident(g17,g0)
    c: Coincident(g18,g19)
    c: Coincident(g19,g20)
    c: Coincident(g20,g21)
    c: Coincident(g21,g22)
    c: Coincident(g22,g23)
    c: Coincident(g23,g18)
    c: Equal(g18, g19-g23) x5
    c: PointOnObject(g18,g24)
    c: PointOnObject(g19,g24)
    c: PointOnObject(g20,g24)
    c: PointOnObject(g21,g24)
    c: PointOnObject(g22,g24)
    c: PointOnObject(g23,g24)
    c: Coincident(g24,g3)
    c: Coincident(g25,g26)
    c: Coincident(g26,g27)
    c: Coincident(g27,g28)
    c: Coincident(g28,g29)
    c: Coincident(g29,g30)
    c: Coincident(g30,g25)
    c: Equal(g25, g26-g30) x5
    c: PointOnObject(g25,g31)
    c: PointOnObject(g26,g31)
    c: PointOnObject(g27,g31)
    c: PointOnObject(g28,g31)
    c: PointOnObject(g29,g31)
    c: PointOnObject(g30,g31)
    c: Coincident(g31,g3)
    c: Equal(g31,g24)
    c: Equal(g24,g17)
    c: Equal(g17,g10)
    c: Horizontal(g20)
    c: Horizontal(g28)
    c: Horizontal(g13)
    c: Horizontal(g9)
    c: DistanceY(g11,g12) = 5.2
FEATURE [PartDesign::Pocket] Pocket002  label="PivNMtCSunk"
  BaseFeature = -> Pocket001
  Length = 2
  Length2 = 100
  Profile = -> Sketch008
  Type = 0
  expr: Length = <<params>>.m25_nut_min_depth
FEATURE [Sketcher::SketchObject] Sketch009
  FullyConstrained = true
  MapMode = 5
  Placement = pos=(0,0,-3) rot=(0,0,1;0rad)
  Support = -> [DatumPlane]
  expr: Constraints[4] = <<params>>.mtplate_circ_inset_offset
  expr: Constraints[1] = <<params>>.bump_diam + 0.6mm
  sketch-geometry (2):
    g0: Circle CenterX=0 CenterY=-100.8 CenterZ=0 NormalX=0 NormalY=0 NormalZ=1 AngleXU=0 Radius=112.8
    g1: GeomPoint X=0 Y=12 Z=0
  constraints (5):
    c: PointOnObject(g0,g-2)
    c: Diameter(g0) = 225.6
    c: PointOnObject(g1,g-2)
    c: PointOnObject(g1,g0)
    c: DistanceY(g-1,g1) = 12
FEATURE [PartDesign::Pocket] Pocket003  label="CircInset"
  BaseFeature = -> Pocket002
  Length = 5
  Length2 = 100
  Profile = -> Sketch009
  Type = 1
FEATURE [PartDesign::Body] Body  label="BumpMtPlate"
  Group = -> [Sketch005,Pad001,DatumPlane,Sketch006,Sketch007,Pocket001,Sketch008,Pocket002,Sketch009,Pocket003]
  Origin = -> Origin001
  Tip = -> Pocket003
FEATURE [App::Part] Part  label="BumperMtPlate_Part"
  Group = -> [Body]
  Origin = -> Origin
FEATURE [Sketcher::SketchObject] Sketch010  label="Sketch_SlidePinRev"
  FullyConstrained = true
  MapMode = 5
  Placement = pos=(0,0,0) rot=(1,0,0;1.5708rad)
  Support = -> [XZ_Plane007]
  expr: Constraints[16] = <<params>>.slidepin_pin_height
  expr: Constraints[15] = <<params>>.slidepin_stop_diam / 2
  expr: Constraints[17] = <<params>>.slidepin_stop_height
  expr: Constraints[14] = <<params>>.slidepin_pin_diam / 2
  expr: Constraints[13] = <<params>>.m2_hole_clear_diam / 2
  sketch-geometry (6):
    g0: LineSegment StartX=1.15 StartY=0 StartZ=0 EndX=2 EndY=0 EndZ=0
    g1: LineSegment StartX=1.15 StartY=0 StartZ=0 EndX=1.15 EndY=-2.7 EndZ=0
    g2: LineSegment StartX=1.15 StartY=-2.7 StartZ=0 EndX=3 EndY=-2.7 EndZ=0
    g3: LineSegment StartX=2 StartY=0 StartZ=0 EndX=2 EndY=-1.5 EndZ=0
    g4: LineSegment StartX=2 StartY=-1.5 StartZ=0 EndX=3 EndY=-1.5 EndZ=0
    g5: LineSegment StartX=3 StartY=-1.5 StartZ=0 EndX=3 EndY=-2.7 EndZ=0
  constraints (18):
    c: PointOnObject(g0,g-1)
    c: PointOnObject(g0,g-1)
    c: Coincident(g1,g0)
    c: Vertical(g1)
    c: Coincident(g2,g1)
    c: Horizontal(g2)
    c: Coincident(g3,g0)
    c: Vertical(g3)
    c: Coincident(g4,g3)
    c: Horizontal(g4)
    c: Coincident(g5,g4)
    c: Coincident(g5,g2)
    c: Vertical(g5)
    c: DistanceX(g-1,g0) = 1.15
    c: DistanceX(g-1,g0) = 2
    c: DistanceX(g-1,g2) = 3
    c: DistanceY(g3,g-1) = 1.5
    c: DistanceY(g2,g4) = 1.2
FEATURE [PartDesign::Revolution] Revolution001
  Angle = 360
  Axis = (0,-2e-16,1)
  Base = (0,0,0)
  Placement = pos=(0,0,0) rot=(1,0,0;1.5708rad)
  Profile = -> Sketch010
  ReferenceAxis = -> Sketch010 [V_Axis]
  Reversed = true
FEATURE [PartDesign::Body] Body003  label="BumpSlidePin"
  Group = -> [Sketch010,Revolution001]
  Origin = -> Origin007
  Placement = pos=(36.8637,22.9647,-10) rot=(0,0,-1;0.261799rad)
  Tip = -> Revolution001
FEATURE [Sketcher::SketchObject] Sketch011  label="Sketch_SlidePinRev001"
  FullyConstrained = true
  MapMode = 5
  Placement = pos=(0,0,0) rot=(1,0,0;1.5708rad)
  Support = -> [XZ_Plane011]
  expr: Constraints[13] = <<params>>.m2_hole_clear_diam / 2
  expr: Constraints[14] = <<params>>.slidepin_pin_diam / 2
  expr: Constraints[17] = <<params>>.slidepin_stop_height
  expr: Constraints[15] = <<params>>.slidepin_stop_diam / 2
  expr: Constraints[16] = <<params>>.slidepin_pin_height
  sketch-geometry (6):
    g0: LineSegment StartX=1.15 StartY=0 StartZ=0 EndX=2 EndY=0 EndZ=0
    g1: LineSegment StartX=1.15 StartY=0 StartZ=0 EndX=1.15 EndY=-2.7 EndZ=0
    g2: LineSegment StartX=1.15 StartY=-2.7 StartZ=0 EndX=3 EndY=-2.7 EndZ=0
    g3: LineSegment StartX=2 StartY=0 StartZ=0 EndX=2 EndY=-1.5 EndZ=0
    g4: LineSegment StartX=2 StartY=-1.5 StartZ=0 EndX=3 EndY=-1.5 EndZ=0
    g5: LineSegment StartX=3 StartY=-1.5 StartZ=0 EndX=3 EndY=-2.7 EndZ=0
  constraints (18):
    c: PointOnObject(g0,g-1)
    c: PointOnObject(g0,g-1)
    c: Coincident(g1,g0)
    c: Vertical(g1)
    c: Coincident(g2,g1)
    c: Horizontal(g2)
    c: Coincident(g3,g0)
    c: Vertical(g3)
    c: Coincident(g4,g3)
    c: Horizontal(g4)
    c: Coincident(g5,g4)
    c: Coincident(g5,g2)
    c: Vertical(g5)
    c: DistanceX(g-1,g0) = 1.15
    c: DistanceX(g-1,g0) = 2
    c: DistanceX(g-1,g2) = 3
    c: DistanceY(g3,g-1) = 1.5
    c: DistanceY(g2,g4) = 1.2
FEATURE [PartDesign::Revolution] Revolution002
  Angle = 360
  Axis = (0,-2e-16,1)
  Base = (0,0,0)
  Placement = pos=(0,0,0) rot=(1,0,0;1.5708rad)
  Profile = -> Sketch011
  ReferenceAxis = -> Sketch011 [V_Axis]
  Reversed = true
FEATURE [PartDesign::Body] Body006  label="SlidePin001"
  Group = -> [Sketch011,Revolution002]
  Origin = -> Origin011
  Placement = pos=(-35.8637,22.9647,-10) rot=(0,0,1;0.261799rad)
  Tip = -> Revolution002
FEATURE [Sketcher::SketchObject] Sketch012  label="Sketch_SlidePinRev002"
  FullyConstrained = true
  MapMode = 5
  Placement = pos=(0,0,0) rot=(1,0,0;1.5708rad)
  Support = -> [XZ_Plane012]
  expr: Constraints[13] = <<params>>.m2_hole_clear_diam / 2
  expr: Constraints[14] = <<params>>.slidepin_pin_diam / 2
  expr: Constraints[17] = <<params>>.slidepin_stop_height
  expr: Constraints[15] = <<params>>.slidepin_stop_diam / 2
  expr: Constraints[16] = <<params>>.slidepin_pin_height
  sketch-geometry (6):
    g0: LineSegment StartX=1.15 StartY=0 StartZ=0 EndX=2 EndY=0 EndZ=0
    g1: LineSegment StartX=1.15 StartY=0 StartZ=0 EndX=1.15 EndY=-2.7 EndZ=0
    g2: LineSegment StartX=1.15 StartY=-2.7 StartZ=0 EndX=3 EndY=-2.7 EndZ=0
    g3: LineSegment StartX=2 StartY=0 StartZ=0 EndX=2 EndY=-1.5 EndZ=0
    g4: LineSegment StartX=2 StartY=-1.5 StartZ=0 EndX=3 EndY=-1.5 EndZ=0
    g5: LineSegment StartX=3 StartY=-1.5 StartZ=0 EndX=3 EndY=-2.7 EndZ=0
  constraints (18):
    c: PointOnObject(g0,g-1)
    c: PointOnObject(g0,g-1)
    c: Coincident(g1,g0)
    c: Vertical(g1)
    c: Coincident(g2,g1)
    c: Horizontal(g2)
    c: Coincident(g3,g0)
    c: Vertical(g3)
    c: Coincident(g4,g3)
    c: Horizontal(g4)
    c: Coincident(g5,g4)
    c: Coincident(g5,g2)
    c: Vertical(g5)
    c: DistanceX(g-1,g0) = 1.15
    c: DistanceX(g-1,g0) = 2
    c: DistanceX(g-1,g2) = 3
    c: DistanceY(g3,g-1) = 1.5
    c: DistanceY(g2,g4) = 1.2
FEATURE [PartDesign::Revolution] Revolution003
  Angle = 360
  Axis = (0,-2e-16,1)
  Base = (0,0,0)
  Placement = pos=(0,0,0) rot=(1,0,0;1.5708rad)
  Profile = -> Sketch012
  ReferenceAxis = -> Sketch012 [V_Axis]
  Reversed = true
FEATURE [PartDesign::Body] Body007  label="SlidePin002"
  Group = -> [Sketch012,Revolution003]
  Origin = -> Origin012
  Placement = pos=(33,3,-10) rot=(0,0,1;0rad)
  Tip = -> Revolution003
FEATURE [Sketcher::SketchObject] Sketch013  label="Sketch_SlidePinRev003"
  FullyConstrained = true
  MapMode = 5
  Placement = pos=(0,0,0) rot=(1,0,0;1.5708rad)
  Support = -> [XZ_Plane013]
  expr: Constraints[13] = <<params>>.m2_hole_clear_diam / 2
  expr: Constraints[14] = <<params>>.slidepin_pin_diam / 2
  expr: Constraints[17] = <<params>>.slidepin_stop_height
  expr: Constraints[15] = <<params>>.slidepin_stop_diam / 2
  expr: Constraints[16] = <<params>>.slidepin_pin_height
  sketch-geometry (6):
    g0: LineSegment StartX=1.15 StartY=0 StartZ=0 EndX=2 EndY=0 EndZ=0
    g1: LineSegment StartX=1.15 StartY=0 StartZ=0 EndX=1.15 EndY=-2.7 EndZ=0
    g2: LineSegment StartX=1.15 StartY=-2.7 StartZ=0 EndX=3 EndY=-2.7 EndZ=0
    g3: LineSegment StartX=2 StartY=0 StartZ=0 EndX=2 EndY=-1.5 EndZ=0
    g4: LineSegment StartX=2 StartY=-1.5 StartZ=0 EndX=3 EndY=-1.5 EndZ=0
    g5: LineSegment StartX=3 StartY=-1.5 StartZ=0 EndX=3 EndY=-2.7 EndZ=0
  constraints (18):
    c: PointOnObject(g0,g-1)
    c: PointOnObject(g0,g-1)
    c: Coincident(g1,g0)
    c: Vertical(g1)
    c: Coincident(g2,g1)
    c: Horizontal(g2)
    c: Coincident(g3,g0)
    c: Vertical(g3)
    c: Coincident(g4,g3)
    c: Horizontal(g4)
    c: Coincident(g5,g4)
    c: Coincident(g5,g2)
    c: Vertical(g5)
    c: DistanceX(g-1,g0) = 1.15
    c: DistanceX(g-1,g0) = 2
    c: DistanceX(g-1,g2) = 3
    c: DistanceY(g3,g-1) = 1.5
    c: DistanceY(g2,g4) = 1.2
FEATURE [PartDesign::Revolution] Revolution004
  Angle = 360
  Axis = (0,-2e-16,1)
  Base = (0,0,0)
  Placement = pos=(0,0,0) rot=(1,0,0;1.5708rad)
  Profile = -> Sketch013
  ReferenceAxis = -> Sketch013 [V_Axis]
  Reversed = true
FEATURE [PartDesign::Body] Body008  label="SlidePin003"
  Group = -> [Sketch013,Revolution004]
  Origin = -> Origin013
  Placement = pos=(-33,4,-10) rot=(0,0,1;0rad)
  Tip = -> Revolution004
FEATURE [App::Part] Part003  label="BumperSlidePin_Part"
  Group = -> [Body003,Body006,Body007,Body008]
  Origin = -> Origin006
  Placement = pos=(0,-3,0) rot=(0,0,1;0rad)
FEATURE [Sketcher::SketchObject] Sketch014
  FullyConstrained = true
  MapMode = 5
  Placement = pos=(0,0,0) rot=(1,0,0;1.5708rad)
  Support = -> [XZ_Plane014]
  expr: Constraints[18] = <<params>>.bump_thick / 4
  expr: Constraints[17] = <<params>>.bump_thick
  expr: Constraints[16] = <<params>>.bump_pivot_inn_diam / 2
  sketch-geometry (7):
    g0: LineSegment StartX=0 StartY=0 StartZ=0 EndX=3.9 EndY=0 EndZ=0
    g1: LineSegment StartX=3.9 StartY=0 StartZ=0 EndX=2.65 EndY=-1.25 EndZ=0
    g2: LineSegment StartX=2.65 StartY=-1.25 StartZ=0 EndX=2.65 EndY=-3.75 EndZ=0
    g3: LineSegment StartX=2.65 StartY=-3.75 StartZ=0 EndX=3.9 EndY=-5 EndZ=0
    g4: LineSegment StartX=3.9 StartY=-5 StartZ=0 EndX=0 EndY=-5 EndZ=0
    g5: LineSegment StartX=0 StartY=-5 StartZ=0 EndX=0 EndY=0 EndZ=0
    g6: LineSegment StartX=3.9 StartY=0 StartZ=0 EndX=3.9 EndY=-5 EndZ=0
  constraints (19):
    c: Coincident(g0,g-1)
    c: PointOnObject(g0,g-1)
    c: Coincident(g1,g0)
    c: Coincident(g2,g1)
    c: Vertical(g2)
    c: Coincident(g3,g2)
    c: Coincident(g4,g3)
    c: PointOnObject(g4,g-2)
    c: Coincident(g5,g4)
    c: Coincident(g5,g0)
    c: Horizontal(g4)
    c: Coincident(g6,g0)
    c: Coincident(g6,g3)
    c: Vertical(g6)
    c: Angle(g0,g1) = 0.785398
    c: Angle(g3,g4) = 0.785398
    c: DistanceX(g4,g2) = 2.65
    c: DistanceY(g4,g0) = 5
    c: DistanceY(g1,g0) = 1.25
FEATURE [Sketcher::SketchObject] Sketch015  label="Sketch_Main_Ext_Temp001"
  FullyConstrained = true
  MapMode = 5
  Support = -> [XY_Plane014]
  expr: Constraints[16] = <<params>>.bump_diam
  expr: Constraints[27] = <<params>>.bump_diam
  expr: Constraints[55] = <<params>>.std_rad
  expr: Constraints[18] = <<params>>.bump_width
  expr: Constraints[35] = <<params>>.bump_slidemt_out_diam
  expr: Constraints[13] = <<params>>.bump_pivot_offset
  expr: Constraints[15] = <<params>>.bump_pivot_out_diam
  expr: Constraints[53] = <<params>>.std_rad
  sketch-geometry (21):
    g0: ArcOfCircle CenterX=0 CenterY=0 CenterZ=0 NormalX=0 NormalY=0 NormalZ=1 AngleXU=0 Radius=4 StartAngle=3.14159 EndAngle=6.28319
    g1: LineSegment StartX=8 StartY=-100.5 StartZ=0 EndX=117.3 EndY=-100.5 EndZ=0
    g2: LineSegment StartX=8 StartY=8.79997 StartZ=0 EndX=8 EndY=12 EndZ=0
    g3: ArcOfCircle CenterX=8 CenterY=-100.5 CenterZ=0 NormalX=0 NormalY=0 NormalZ=1 AngleXU=0 Radius=109.3 StartAngle=1.34622 EndAngle=1.5708
    g4: ArcOfCircle CenterX=8 CenterY=-100.5 CenterZ=0 NormalX=0 NormalY=0 NormalZ=1 AngleXU=0 Radius=112.5 StartAngle=0.349066 EndAngle=1.5708
    g5: LineSegment StartX=8 StartY=8.79997 StartZ=0 EndX=8 EndY=0 EndZ=0
    g6: LineSegment StartX=8 StartY=-100.5 StartZ=0 EndX=8 EndY=0 EndZ=0
    g7: ArcOfCircle CenterX=8 CenterY=-100.5 CenterZ=0 NormalX=0 NormalY=0 NormalZ=1 AngleXU=0 Radius=109.3 StartAngle=0.349066 EndAngle=1.27177
    g8: LineSegment StartX=8 StartY=-100.5 StartZ=0 EndX=36.2889 EndY=5.07567 EndZ=0
    g9: LineSegment StartX=8 StartY=-100.5 StartZ=0 EndX=110.708 EndY=-63.1172 EndZ=0
    g10: LineSegment StartX=110.708 StartY=-63.1172 StartZ=0 EndX=113.715 EndY=-62.0228 EndZ=0
    g11: Circle CenterX=8 CenterY=-100.5 CenterZ=0 NormalX=0 NormalY=0 NormalZ=1 AngleXU=0 Radius=112.5
    g12: Circle CenterX=8 CenterY=-100.5 CenterZ=0 NormalX=0 NormalY=0 NormalZ=1 AngleXU=0 Radius=109.3
    g13: ArcOfCircle CenterX=36.2889 CenterY=5.07567 CenterZ=0 NormalX=0 NormalY=0 NormalZ=1 AngleXU=0 Radius=2.5 StartAngle=3.35887 EndAngle=5.54231
    g14: ArcOfCircle CenterX=112.212 CenterY=-62.57 CenterZ=0 NormalX=0 NormalY=0 NormalZ=1 AngleXU=0 Radius=1.6 StartAngle=3.49066 EndAngle=6.63225
    g15: ArcOfCircle CenterX=7.99997 CenterY=1.02572e-07 CenterZ=0 NormalX=0 NormalY=0 NormalZ=1 AngleXU=0 Radius=12 StartAngle=1.57079 EndAngle=3.14159
    g16: ArcOfCircle CenterX=0 CenterY=0 CenterZ=0 NormalX=0 NormalY=0 NormalZ=1 AngleXU=0 Radius=4 StartAngle=0 EndAngle=0.976409
    g17: ArcOfCircle CenterX=7.99997 CenterY=1.02572e-07 CenterZ=0 NormalX=0 NormalY=0 NormalZ=1 AngleXU=0 Radius=8.79997 StartAngle=1.57079 EndAngle=2.32177
    g18: ArcOfCircle CenterX=3.36001 CenterY=4.97095 CenterZ=0 NormalX=0 NormalY=0 NormalZ=1 AngleXU=0 Radius=2 StartAngle=2.32177 EndAngle=4.118
    g19: ArcOfCircle CenterX=31.8947 CenterY=4.10558 CenterZ=0 NormalX=0 NormalY=0 NormalZ=1 AngleXU=0 Radius=2 StartAngle=0.217281 EndAngle=1.34622
    g20: ArcOfCircle CenterX=39.6094 CenterY=2.03845 CenterZ=0 NormalX=0 NormalY=0 NormalZ=1 AngleXU=0 Radius=2 StartAngle=1.27177 EndAngle=2.40071
  constraints (57):
    c: Coincident(g0,g-1)
    c: PointOnObject(g0,g-1)
    c: PointOnObject(g0,g-1)
    c: Horizontal(g1)
    c: Vertical(g2)
    c: Coincident(g4,g3)
    c: Coincident(g4,g2)
    c: Coincident(g5,g3)
    c: PointOnObject(g5,g-1)
    c: Vertical(g5)
    c: Coincident(g6,g3)
    c: Coincident(g6,g5)
    c: Vertical(g6)
    c: DistanceX(g0,g5) = 8
    c: Coincident(g2,g3)
    c: Diameter(g0) = 8
    c: Diameter(g4) = 225
    c: Coincident(g1,g3)
    c: DistanceY(g3,g4) = 3.2
    c: Coincident(g7,g3)
    c: Coincident(g8,g3)
    c: Coincident(g9,g3)
    c: Coincident(g9,g7)
    c: Coincident(g10,g7)
    c: Coincident(g10,g4)
    c: Parallel(g9,g10)
    c: Coincident(g11,g3)
    c: Diameter(g11) = 225
    c: Coincident(g12,g3)
    c: PointOnObject(g3,g12)
    c: PointOnObject(g13,g12)
    c: Coincident(g8,g13)
    c: PointOnObject(g14,g10)
    c: Coincident(g14,g7)
    c: Coincident(g14,g4)
    c: Diameter(g13) = 5
    c: Coincident(g15,g4)
    c: Coincident(g15,g0)
    c: Coincident(g16,g0)
    c: Coincident(g17,g15)
    c: Coincident(g17,g3)
    c: Coincident(g16,g0)
    c: PointOnObject(g1,g12)
    c: Angle(g1,g9) = 0.349066
    c: Angle(g8,g6) = 0.261799
    c: Tangent(g0,g15)
    c: Tangent(g15,g4)
    c: Tangent(g16,g18) = 1.5708
    c: Tangent(g17,g18) = -1.5708
    c: Tangent(g13,g19) = 1.5708
    c: Tangent(g3,g19) = -1.5708
    c: Tangent(g13,g20) = 1.5708
    c: Tangent(g7,g20) = -1.5708
    c: Radius(g18) = 2
    c: Equal(g19,g20)
    c: Radius(g20) = 2
    c: PointOnObject(g7,g12)
FEATURE [Sketcher::SketchObject] Sketch016  label="Sketch_SlideHole001"
  FullyConstrained = true
  MapMode = 5
  Support = -> [XY_Plane014]
  expr: Constraints[58] = <<params>>.m2_hole_clear_diam
  expr: Constraints[15] = <<params>>.bump_pivot_out_diam
  expr: Constraints[53] = <<params>>.std_rad
  expr: Constraints[13] = <<params>>.bump_pivot_offset
  expr: Constraints[35] = <<params>>.bump_slidemt_out_diam
  expr: Constraints[18] = <<params>>.bump_width
  expr: Constraints[55] = <<params>>.std_rad
  expr: Constraints[27] = <<params>>.bump_diam
  expr: Constraints[44] = <<params>>.bump_piv_ang
  expr: Constraints[16] = <<params>>.bump_diam
  sketch-geometry (22):
    g0: ArcOfCircle CenterX=0 CenterY=0 CenterZ=0 NormalX=0 NormalY=0 NormalZ=1 AngleXU=0 Radius=4 StartAngle=3.14159 EndAngle=6.28319
    g1: LineSegment StartX=8 StartY=-100.5 StartZ=0 EndX=117.3 EndY=-100.5 EndZ=0
    g2: LineSegment StartX=8 StartY=8.8 StartZ=0 EndX=8 EndY=12 EndZ=0
    g3: ArcOfCircle CenterX=8 CenterY=-100.5 CenterZ=0 NormalX=0 NormalY=0 NormalZ=1 AngleXU=0 Radius=109.3 StartAngle=1.39858 EndAngle=1.5708
    g4: ArcOfCircle CenterX=8 CenterY=-100.5 CenterZ=0 NormalX=0 NormalY=0 NormalZ=1 AngleXU=0 Radius=112.5 StartAngle=0.349066 EndAngle=1.5708
    g5: LineSegment StartX=8 StartY=8.8 StartZ=0 EndX=8 EndY=0 EndZ=0
    g6: LineSegment StartX=8 StartY=-100.5 StartZ=0 EndX=8 EndY=0 EndZ=0
    g7: ArcOfCircle CenterX=8 CenterY=-100.5 CenterZ=0 NormalX=0 NormalY=0 NormalZ=1 AngleXU=0 Radius=109.3 StartAngle=0.349066 EndAngle=1.32413
    g8: LineSegment StartX=8 StartY=-100.5 StartZ=0 EndX=30.7247 EndY=6.41153 EndZ=0
    g9: LineSegment StartX=8 StartY=-100.5 StartZ=0 EndX=110.708 EndY=-63.1172 EndZ=0
    g10: LineSegment StartX=110.708 StartY=-63.1172 StartZ=0 EndX=113.715 EndY=-62.0227 EndZ=0
    g11: Circle CenterX=8 CenterY=-100.5 CenterZ=0 NormalX=0 NormalY=0 NormalZ=1 AngleXU=0 Radius=112.5
    g12: Circle CenterX=8 CenterY=-100.5 CenterZ=0 NormalX=0 NormalY=0 NormalZ=1 AngleXU=0 Radius=109.3
    g13: ArcOfCircle CenterX=30.7247 CenterY=6.41153 CenterZ=0 NormalX=0 NormalY=0 NormalZ=1 AngleXU=0 Radius=2.5 StartAngle=3.41123 EndAngle=5.59466
    g14: ArcOfCircle CenterX=112.212 CenterY=-62.57 CenterZ=0 NormalX=0 NormalY=0 NormalZ=1 AngleXU=0 Radius=1.6 StartAngle=3.49066 EndAngle=6.63225
    g15: ArcOfCircle CenterX=8 CenterY=-2.29801e-07 CenterZ=0 NormalX=0 NormalY=0 NormalZ=1 AngleXU=0 Radius=12 StartAngle=1.5708 EndAngle=3.14159
    g16: ArcOfCircle CenterX=0 CenterY=0 CenterZ=0 NormalX=0 NormalY=0 NormalZ=1 AngleXU=0 Radius=4 StartAngle=0 EndAngle=0.976411
    g17: ArcOfCircle CenterX=8 CenterY=-2.29801e-07 CenterZ=0 NormalX=0 NormalY=0 NormalZ=1 AngleXU=0 Radius=8.8 StartAngle=1.5708 EndAngle=2.32177
    g18: ArcOfCircle CenterX=3.36 CenterY=4.97096 CenterZ=0 NormalX=0 NormalY=0 NormalZ=1 AngleXU=0 Radius=2 StartAngle=2.32177 EndAngle=4.118
    g19: ArcOfCircle CenterX=26.3873 CenterY=5.2128 CenterZ=0 NormalX=0 NormalY=0 NormalZ=1 AngleXU=0 Radius=2 StartAngle=0.269641 EndAngle=1.39858
    g20: ArcOfCircle CenterX=34.1996 CenterY=3.55226 CenterZ=0 NormalX=0 NormalY=0 NormalZ=1 AngleXU=0 Radius=2 StartAngle=1.32413 EndAngle=2.45307
    g21: Circle CenterX=30.7247 CenterY=6.41153 CenterZ=0 NormalX=0 NormalY=0 NormalZ=1 AngleXU=0 Radius=1.15
  constraints (59):
    c: Coincident(g0,g-1)
    c: PointOnObject(g0,g-1)
    c: PointOnObject(g0,g-1)
    c: Horizontal(g1)
    c: Vertical(g2)
    c: Coincident(g4,g3)
    c: Coincident(g4,g2)
    c: Coincident(g5,g3)
    c: PointOnObject(g5,g-1)
    c: Vertical(g5)
    c: Coincident(g6,g3)
    c: Coincident(g6,g5)
    c: Vertical(g6)
    c: DistanceX(g0,g5) = 8
    c: Coincident(g2,g3)
    c: Diameter(g0) = 8
    c: Diameter(g4) = 225
    c: Coincident(g1,g3)
    c: DistanceY(g3,g4) = 3.2
    c: Coincident(g7,g3)
    c: Coincident(g8,g3)
    c: Coincident(g9,g3)
    c: Coincident(g9,g7)
    c: Coincident(g10,g7)
    c: Coincident(g10,g4)
    c: Parallel(g9,g10)
    c: Coincident(g11,g3)
    c: Diameter(g11) = 225
    c: Coincident(g12,g3)
    c: PointOnObject(g3,g12)
    c: PointOnObject(g13,g12)
    c: Coincident(g8,g13)
    c: PointOnObject(g14,g10)
    c: Coincident(g14,g7)
    c: Coincident(g14,g4)
    c: Diameter(g13) = 5
    c: Coincident(g15,g4)
    c: Coincident(g15,g0)
    c: Coincident(g16,g0)
    c: Coincident(g17,g15)
    c: Coincident(g17,g3)
    c: Coincident(g16,g0)
    c: PointOnObject(g1,g12)
    c: Angle(g1,g9) = 0.349066
    c: Angle(g8,g6) = 0.20944
    c: Tangent(g0,g15)
    c: Tangent(g15,g4)
    c: Tangent(g16,g18) = 1.5708
    c: Tangent(g17,g18) = -1.5708
    c: Tangent(g13,g19) = 1.5708
    c: Tangent(g3,g19) = -1.5708
    c: Tangent(g13,g20) = 1.5708
    c: Tangent(g7,g20) = -1.5708
    c: Radius(g18) = 2
    c: Equal(g19,g20)
    c: Radius(g20) = 2
    c: PointOnObject(g7,g12)
    c: Coincident(g21,g8)
    c: Diameter(g21) = 2.3
FEATURE [Sketcher::SketchObject] Sketch017  label="Sketch_Main_Ext001"
  FullyConstrained = true
  MapMode = 5
  Support = -> [XY_Plane014]
  expr: Constraints[53] = <<params>>.std_rad
  expr: Constraints[15] = <<params>>.bump_pivot_out_diam
  expr: Constraints[13] = <<params>>.bump_pivot_offset
  expr: Constraints[35] = <<params>>.bump_slidemt_out_diam
  expr: Constraints[43] = 90 - <<params>>.bump_sweep_ang
  expr: Constraints[18] = <<params>>.bump_width
  expr: Constraints[55] = <<params>>.std_rad
  expr: Constraints[27] = <<params>>.bump_diam
  expr: Constraints[44] = <<params>>.bump_piv_ang
  expr: Constraints[16] = <<params>>.bump_diam
  sketch-geometry (21):
    g0: ArcOfCircle CenterX=0 CenterY=0 CenterZ=0 NormalX=0 NormalY=0 NormalZ=1 AngleXU=0 Radius=4 StartAngle=3.14159 EndAngle=6.28319
    g1: LineSegment StartX=8 StartY=-100.5 StartZ=0 EndX=117.3 EndY=-100.5 EndZ=0
    g2: LineSegment StartX=8 StartY=8.80001 StartZ=0 EndX=8 EndY=12 EndZ=0
    g3: ArcOfCircle CenterX=8 CenterY=-100.5 CenterZ=0 NormalX=0 NormalY=0 NormalZ=1 AngleXU=0 Radius=109.3 StartAngle=1.39858 EndAngle=1.5708
    g4: ArcOfCircle CenterX=8 CenterY=-100.5 CenterZ=0 NormalX=0 NormalY=0 NormalZ=1 AngleXU=0 Radius=112.5 StartAngle=0.785398 EndAngle=1.5708
    g5: LineSegment StartX=8 StartY=8.80001 StartZ=0 EndX=8 EndY=0 EndZ=0
    g6: LineSegment StartX=8 StartY=-100.5 StartZ=0 EndX=8 EndY=0 EndZ=0
    g7: ArcOfCircle CenterX=8 CenterY=-100.5 CenterZ=0 NormalX=0 NormalY=0 NormalZ=1 AngleXU=0 Radius=109.3 StartAngle=0.785398 EndAngle=1.32413
    g8: LineSegment StartX=8 StartY=-100.5 StartZ=0 EndX=30.7247 EndY=6.41154 EndZ=0
    g9: LineSegment StartX=8 StartY=-100.5 StartZ=0 EndX=85.2868 EndY=-23.2132 EndZ=0
    g10: LineSegment StartX=85.2868 StartY=-23.2132 StartZ=0 EndX=87.5495 EndY=-20.9505 EndZ=0
    g11: Circle CenterX=8 CenterY=-100.5 CenterZ=0 NormalX=0 NormalY=0 NormalZ=1 AngleXU=0 Radius=112.5
    g12: Circle CenterX=8 CenterY=-100.5 CenterZ=0 NormalX=0 NormalY=0 NormalZ=1 AngleXU=0 Radius=109.3
    g13: ArcOfCircle CenterX=30.7247 CenterY=6.41154 CenterZ=0 NormalX=0 NormalY=0 NormalZ=1 AngleXU=0 Radius=2.5 StartAngle=3.41123 EndAngle=5.59466
    g14: ArcOfCircle CenterX=86.4181 CenterY=-22.0819 CenterZ=0 NormalX=0 NormalY=0 NormalZ=1 AngleXU=0 Radius=1.6 StartAngle=3.92699 EndAngle=7.06858
    g15: ArcOfCircle CenterX=8.00001 CenterY=6.82085e-07 CenterZ=0 NormalX=0 NormalY=0 NormalZ=1 AngleXU=0 Radius=12 StartAngle=1.5708 EndAngle=3.14159
    g16: ArcOfCircle CenterX=0 CenterY=0 CenterZ=0 NormalX=0 NormalY=0 NormalZ=1 AngleXU=0 Radius=4 StartAngle=0 EndAngle=0.976411
    g17: ArcOfCircle CenterX=8.00001 CenterY=6.82085e-07 CenterZ=0 NormalX=0 NormalY=0 NormalZ=1 AngleXU=0 Radius=8.80001 StartAngle=1.5708 EndAngle=2.32177
    g18: ArcOfCircle CenterX=3.36 CenterY=4.97096 CenterZ=0 NormalX=0 NormalY=0 NormalZ=1 AngleXU=0 Radius=2 StartAngle=2.32177 EndAngle=4.118
    g19: ArcOfCircle CenterX=26.3873 CenterY=5.2128 CenterZ=0 NormalX=0 NormalY=0 NormalZ=1 AngleXU=0 Radius=2 StartAngle=0.269641 EndAngle=1.39858
    g20: ArcOfCircle CenterX=34.1996 CenterY=3.55226 CenterZ=0 NormalX=0 NormalY=0 NormalZ=1 AngleXU=0 Radius=2 StartAngle=1.32413 EndAngle=2.45307
  constraints (57):
    c: Coincident(g0,g-1)
    c: PointOnObject(g0,g-1)
    c: PointOnObject(g0,g-1)
    c: Horizontal(g1)
    c: Vertical(g2)
    c: Coincident(g4,g3)
    c: Coincident(g4,g2)
    c: Coincident(g5,g3)
    c: PointOnObject(g5,g-1)
    c: Vertical(g5)
    c: Coincident(g6,g3)
    c: Coincident(g6,g5)
    c: Vertical(g6)
    c: DistanceX(g0,g5) = 8
    c: Coincident(g2,g3)
    c: Diameter(g0) = 8
    c: Diameter(g4) = 225
    c: Coincident(g1,g3)
    c: DistanceY(g3,g4) = 3.2
    c: Coincident(g7,g3)
    c: Coincident(g8,g3)
    c: Coincident(g9,g3)
    c: Coincident(g9,g7)
    c: Coincident(g10,g7)
    c: Coincident(g10,g4)
    c: Parallel(g9,g10)
    c: Coincident(g11,g3)
    c: Diameter(g11) = 225
    c: Coincident(g12,g3)
    c: PointOnObject(g3,g12)
    c: PointOnObject(g13,g12)
    c: Coincident(g8,g13)
    c: PointOnObject(g14,g10)
    c: Coincident(g14,g7)
    c: Coincident(g14,g4)
    c: Diameter(g13) = 5
    c: Coincident(g15,g4)
    c: Coincident(g15,g0)
    c: Coincident(g16,g0)
    c: Coincident(g17,g15)
    c: Coincident(g17,g3)
    c: Coincident(g16,g0)
    c: PointOnObject(g1,g12)
    c: Angle(g1,g9) = 0.785398
    c: Angle(g8,g6) = 0.20944
    c: Tangent(g0,g15)
    c: Tangent(g15,g4)
    c: Tangent(g16,g18) = 1.5708
    c: Tangent(g17,g18) = -1.5708
    c: Tangent(g13,g19) = 1.5708
    c: Tangent(g3,g19) = -1.5708
    c: Tangent(g13,g20) = 1.5708
    c: Tangent(g7,g20) = -1.5708
    c: Radius(g18) = 2
    c: Equal(g19,g20)
    c: Radius(g20) = 2
    c: PointOnObject(g7,g12)
FEATURE [PartDesign::Pad] Pad002  label="MainExt001"
  Direction = (1,1,1)
  Length = 5
  Length2 = 100
  Profile = -> Sketch017
  Reversed = true
  Type = 0
  expr: Length = <<params>>.bump_thick
FEATURE [PartDesign::Pocket] Pocket004  label="SlideMtHole001"
  BaseFeature = -> Pad002
  Length = 5
  Length2 = 100
  Midplane = true
  Profile = -> Sketch016
  Type = 1
FEATURE [PartDesign::Groove] Groove001
  Angle = 360
  Axis = (0,-2e-16,1)
  Base = (0,0,0)
  BaseFeature = -> Pocket004
  Profile = -> Sketch014
  ReferenceAxis = -> Sketch014 [V_Axis]
FEATURE [PartDesign::Body] Body009  label="BumperWhisker001"
  Group = -> [Sketch017,Pad002,Sketch015,Sketch016,Pocket004,Sketch014,Groove001]
  Origin = -> Origin014
  Placement = pos=(-10,0,-11) rot=(-0.043619,0.999048,0;3.14159rad)
  Tip = -> Groove001
FEATURE [Sketcher::SketchObject] Sketch018
  FullyConstrained = true
  MapMode = 5
  Placement = pos=(0,0,0) rot=(1,0,0;1.5708rad)
  Support = -> [XZ_Plane015]
  expr: Constraints[21] = (<<params>>.bump_pivot_inn_diam - <<params>>.bump_pivot_tol) / 2
  expr: Constraints[22] = <<params>>.m25_hole_clear_diam / 2
  expr: Constraints[14] = <<params>>.bump_pivot_height_tol
  expr: Constraints[13] = <<params>>.bump_pivot_plate_thick
  expr: Constraints[16] = <<params>>.bump_thick
  expr: Constraints[20] = <<params>>.bump_pivot_out_diam / 2
  expr: Constraints[15] = <<params>>.bump_thick / 4
  sketch-geometry (8):
    g0: LineSegment StartX=1.4 StartY=0.3 StartZ=0 EndX=2.5 EndY=0.3 EndZ=0
    g1: LineSegment StartX=2.5 StartY=0.3 StartZ=0 EndX=2.5 EndY=-3.75 EndZ=0
    g2: LineSegment StartX=2.5 StartY=-3.75 StartZ=0 EndX=3.75 EndY=-5 EndZ=0
    g3: LineSegment StartX=3.75 StartY=-5 StartZ=0 EndX=4 EndY=-5 EndZ=0
    g4: LineSegment StartX=4 StartY=-5 StartZ=0 EndX=4 EndY=-6.6 EndZ=0
    g5: LineSegment StartX=4 StartY=-6.6 StartZ=0 EndX=1.4 EndY=-6.6 EndZ=0
    g6: LineSegment StartX=3.75 StartY=-5 StartZ=0 EndX=0 EndY=-5 EndZ=0
    g7: LineSegment StartX=1.4 StartY=0.3 StartZ=0 EndX=1.4 EndY=-6.6 EndZ=0
  constraints (24):
    c: Horizontal(g0)
    c: Coincident(g1,g0)
    c: Vertical(g1)
    c: Coincident(g2,g1)
    c: Coincident(g3,g2)
    c: Horizontal(g3)
    c: Coincident(g4,g3)
    c: Vertical(g4)
    c: Coincident(g5,g4)
    c: Horizontal(g5)
    c: Coincident(g6,g2)
    c: Horizontal(g6)
    c: Angle(g2,g6) = 0.785398
    c: DistanceY(g4,g3) = 1.6
    c: DistanceY(g-1,g0) = 0.3
    c: DistanceY(g2,g1) = 1.25
    c: DistanceY(g2,g-1) = 5
    c: Coincident(g7,g0)
    c: Coincident(g7,g5)
    c: Vertical(g7)
    c: DistanceX(g-1,g4) = 4
    c: DistanceX(g-1,g0) = 2.5
    c: DistanceX(g-1,g0) = 1.4
    c: PointOnObject(g6,g-2)
FEATURE [PartDesign::Revolution] Revolution005
  Angle = 360
  Axis = (0,-2e-16,1)
  Base = (0,0,0)
  Placement = pos=(0,0,0) rot=(1,0,0;1.5708rad)
  Profile = -> Sketch018
  ReferenceAxis = -> Sketch018 [V_Axis]
  Reversed = true
FEATURE [PartDesign::Body] Body010  label="BumpPivot001"
  Group = -> [Sketch018,Revolution005]
  Origin = -> Origin015
  Placement = pos=(-10,0,-6) rot=(0,0,1;0rad)
  Tip = -> Revolution005
FEATURE [App::Part] Part001  label="BumperWhisker_Part"
  Group = -> [Body001,Body005,Body009,Body010]
  Origin = -> Origin002
  Placement = pos=(5,16,1) rot=(0,0,1;0rad)
FEATURE [Sketcher::SketchObject] Sketch019
  FullyConstrained = true
  MapMode = 5
  Support = -> [XY_Plane005]
  expr: Constraints[38] = <<params>>.slide_hoop_width
  expr: Constraints[20] = <<params>>.slide_leng
  expr: Constraints[23] = <<params>>.slide_leng / 2
  expr: Constraints[19] = <<params>>.slide_internal_width + 2 * <<params>>.slide_hoop_width
  expr: Constraints[18] = <<params>>.slide_maj_rad
  sketch-geometry (15):
    g0: ArcOfCircle CenterX=112.5 CenterY=0 CenterZ=0 NormalX=0 NormalY=0 NormalZ=1 AngleXU=0 Radius=116.25 StartAngle=3.05259 EndAngle=3.2306
    g1: ArcOfCircle CenterX=112.5 CenterY=0 CenterZ=0 NormalX=0 NormalY=0 NormalZ=1 AngleXU=0 Radius=108.75 StartAngle=3.05259 EndAngle=3.2306
    g2: LineSegment StartX=112.5 StartY=0 StartZ=0 EndX=-3.28983 EndY=10.3333 EndZ=0
    g3: LineSegment StartX=112.5 StartY=0 StartZ=0 EndX=-3.28983 EndY=-10.3333 EndZ=0
    g4: GeomPoint X=-3.75 Y=0 Z=0
    g5: GeomPoint X=3.75 Y=0 Z=0
    g6: GeomPoint X=0.445326 Y=10 Z=0
    g7: GeomPoint X=0.445326 Y=-10 Z=0
    g8: ArcOfCircle CenterX=0.445326 CenterY=10 CenterZ=0 NormalX=0 NormalY=0 NormalZ=1 AngleXU=0 Radius=3.75 StartAngle=6.19418 EndAngle=9.33577
    g9: ArcOfCircle CenterX=0.445326 CenterY=-10 CenterZ=0 NormalX=0 NormalY=0 NormalZ=1 AngleXU=0 Radius=3.75 StartAngle=3.2306 EndAngle=6.37219
    g10: ArcOfCircle CenterX=0.445326 CenterY=10 CenterZ=0 NormalX=0 NormalY=0 NormalZ=1 AngleXU=0 Radius=2.15 StartAngle=6.19418 EndAngle=9.33577
    g11: ArcOfCircle CenterX=0.445326 CenterY=-10 CenterZ=0 NormalX=0 NormalY=0 NormalZ=1 AngleXU=0 Radius=2.15 StartAngle=3.2306 EndAngle=6.37219
    g12: ArcOfCircle CenterX=112.5 CenterY=0 CenterZ=0 NormalX=0 NormalY=0 NormalZ=1 AngleXU=0 Radius=114.65 StartAngle=3.05259 EndAngle=3.2306
    g13: ArcOfCircle CenterX=112.5 CenterY=0 CenterZ=0 NormalX=0 NormalY=0 NormalZ=1 AngleXU=0 Radius=110.35 StartAngle=3.05259 EndAngle=3.2306
    g14: GeomPoint X=-2.15 Y=0 Z=0
  constraints (39):
    c: PointOnObject(g0,g-1)
    c: Coincident(g1,g0)
    c: Coincident(g2,g0)
    c: Coincident(g2,g0)
    c: Coincident(g3,g0)
    c: Coincident(g3,g0)
    c: PointOnObject(g4,g-1)
    c: PointOnObject(g5,g1)
    c: PointOnObject(g4,g0)
    c: Symmetric(g4,g5,g-1)
    c: PointOnObject(g1,g2)
    c: PointOnObject(g1,g3)
    c: Symmetric(g0,g1,g6)
    c: Symmetric(g0,g1,g7)
    c: Coincident(g8,g6)
    c: Coincident(g8,g0)
    c: Coincident(g9,g7)
    c: Coincident(g9,g0)
    c: DistanceX(g-1,g0) = 112.5
    c: DistanceX(g4,g5) = 7.5
    c: DistanceY(g9,g8) = 20
    c: PointOnObject(g8,g2)
    c: PointOnObject(g9,g3)
    c: DistanceY(g9,g-1) = 10
    c: Coincident(g10,g8)
    c: PointOnObject(g10,g2)
    c: PointOnObject(g10,g2)
    c: Coincident(g11,g9)
    c: PointOnObject(g11,g3)
    c: PointOnObject(g11,g3)
    c: Coincident(g12,g0)
    c: Coincident(g12,g10)
    c: Coincident(g12,g11)
    c: Coincident(g13,g0)
    c: Coincident(g13,g10)
    c: PointOnObject(g13,g3)
    c: PointOnObject(g14,g-1)
    c: PointOnObject(g14,g12)
    c: DistanceX(g4,g14) = 1.6
FEATURE [PartDesign::Pad] Pad003  label="MainSlideExt"
  Direction = (1,1,1)
  Length = 1.2
  Length2 = 100
  Profile = -> Sketch019
  Reversed = true
  Type = 0
  expr: Length = <<params>>.slide_thickness
FEATURE [PartDesign::Body] Body002  label="BumpSlide"
  Group = -> [Sketch019,Pad003]
  Origin = -> Origin005
  Placement = pos=(34.6071,13.5094,-10) rot=(0,0,-1;0.174533rad)
  Tip = -> Pad003
FEATURE [Sketcher::SketchObject] Sketch020
  FullyConstrained = true
  MapMode = 5
  Support = -> [XY_Plane016]
  expr: Constraints[18] = <<params>>.slide_maj_rad
  expr: Constraints[19] = <<params>>.slide_internal_width + 2 * <<params>>.slide_hoop_width
  expr: Constraints[23] = <<params>>.slide_leng / 2
  expr: Constraints[20] = <<params>>.slide_leng
  expr: Constraints[38] = <<params>>.slide_hoop_width
  sketch-geometry (15):
    g0: ArcOfCircle CenterX=112.5 CenterY=0 CenterZ=0 NormalX=0 NormalY=0 NormalZ=1 AngleXU=0 Radius=116.25 StartAngle=3.05259 EndAngle=3.2306
    g1: ArcOfCircle CenterX=112.5 CenterY=0 CenterZ=0 NormalX=0 NormalY=0 NormalZ=1 AngleXU=0 Radius=108.75 StartAngle=3.05259 EndAngle=3.2306
    g2: LineSegment StartX=112.5 StartY=0 StartZ=0 EndX=-3.28983 EndY=10.3333 EndZ=0
    g3: LineSegment StartX=112.5 StartY=0 StartZ=0 EndX=-3.28983 EndY=-10.3333 EndZ=0
    g4: GeomPoint X=-3.75 Y=0 Z=0
    g5: GeomPoint X=3.75 Y=0 Z=0
    g6: GeomPoint X=0.445326 Y=10 Z=0
    g7: GeomPoint X=0.445326 Y=-10 Z=0
    g8: ArcOfCircle CenterX=0.445326 CenterY=10 CenterZ=0 NormalX=0 NormalY=0 NormalZ=1 AngleXU=0 Radius=3.75 StartAngle=6.19418 EndAngle=9.33577
    g9: ArcOfCircle CenterX=0.445326 CenterY=-10 CenterZ=0 NormalX=0 NormalY=0 NormalZ=1 AngleXU=0 Radius=3.75 StartAngle=3.2306 EndAngle=6.37219
    g10: ArcOfCircle CenterX=0.445326 CenterY=10 CenterZ=0 NormalX=0 NormalY=0 NormalZ=1 AngleXU=0 Radius=2.15 StartAngle=6.19418 EndAngle=9.33577
    g11: ArcOfCircle CenterX=0.445326 CenterY=-10 CenterZ=0 NormalX=0 NormalY=0 NormalZ=1 AngleXU=0 Radius=2.15 StartAngle=3.2306 EndAngle=6.37219
    g12: ArcOfCircle CenterX=112.5 CenterY=0 CenterZ=0 NormalX=0 NormalY=0 NormalZ=1 AngleXU=0 Radius=114.65 StartAngle=3.05259 EndAngle=3.2306
    g13: ArcOfCircle CenterX=112.5 CenterY=0 CenterZ=0 NormalX=0 NormalY=0 NormalZ=1 AngleXU=0 Radius=110.35 StartAngle=3.05259 EndAngle=3.2306
    g14: GeomPoint X=-2.15 Y=0 Z=0
  constraints (39):
    c: PointOnObject(g0,g-1)
    c: Coincident(g1,g0)
    c: Coincident(g2,g0)
    c: Coincident(g2,g0)
    c: Coincident(g3,g0)
    c: Coincident(g3,g0)
    c: PointOnObject(g4,g-1)
    c: PointOnObject(g5,g1)
    c: PointOnObject(g4,g0)
    c: Symmetric(g4,g5,g-1)
    c: PointOnObject(g1,g2)
    c: PointOnObject(g1,g3)
    c: Symmetric(g0,g1,g6)
    c: Symmetric(g0,g1,g7)
    c: Coincident(g8,g6)
    c: Coincident(g8,g0)
    c: Coincident(g9,g7)
    c: Coincident(g9,g0)
    c: DistanceX(g-1,g0) = 112.5
    c: DistanceX(g4,g5) = 7.5
    c: DistanceY(g9,g8) = 20
    c: PointOnObject(g8,g2)
    c: PointOnObject(g9,g3)
    c: DistanceY(g9,g-1) = 10
    c: Coincident(g10,g8)
    c: PointOnObject(g10,g2)
    c: PointOnObject(g10,g2)
    c: Coincident(g11,g9)
    c: PointOnObject(g11,g3)
    c: PointOnObject(g11,g3)
    c: Coincident(g12,g0)
    c: Coincident(g12,g10)
    c: Coincident(g12,g11)
    c: Coincident(g13,g0)
    c: Coincident(g13,g10)
    c: PointOnObject(g13,g3)
    c: PointOnObject(g14,g-1)
    c: PointOnObject(g14,g12)
    c: DistanceX(g4,g14) = 1.6
FEATURE [PartDesign::Pad] Pad004  label="MainSlideExt001"
  Direction = (1,1,1)
  Length = 1.2
  Length2 = 100
  Profile = -> Sketch020
  Reversed = true
  Type = 0
  expr: Length = <<params>>.slide_thickness
FEATURE [PartDesign::Body] Body011  label="BumperSlide001"
  Group = -> [Sketch020,Pad004]
  Origin = -> Origin016
  Placement = pos=(-34.1433,13.6375,-11) rot=(-0.087156,0.996195,0;3.14159rad)
  Tip = -> Pad004
FEATURE [App::Part] Part002  label="BumperSlide_Part"
  Group = -> [Body002,Body011]
  Origin = -> Origin004
  Placement = pos=(0,-3,0) rot=(0,0,1;0rad)
FEATURE [Sketcher::SketchObject] Sketch021
  FullyConstrained = true
  MapMode = 5
  Support = -> [XY_Plane009]
  expr: Constraints[3] = <<params>>.pinoffset_diam
  expr: Constraints[2] = <<params>>.m25_hole_clear_diam
  sketch-geometry (2):
    g0: Circle CenterX=0 CenterY=0 CenterZ=0 NormalX=0 NormalY=0 NormalZ=1 AngleXU=0 Radius=3
    g1: Circle CenterX=0 CenterY=0 CenterZ=0 NormalX=0 NormalY=0 NormalZ=1 AngleXU=0 Radius=1.4
  constraints (4):
    c: Coincident(g0,g-1)
    c: Coincident(g1,g0)
    c: Diameter(g1) = 2.8
    c: Diameter(g0) = 6
FEATURE [PartDesign::Pad] Pad005  label="MainStandOffExt"
  Direction = (1,1,1)
  Length = 5
  Length2 = 100
  Profile = -> Sketch021
  Reversed = true
  Type = 0
  expr: Length = <<params>>.pinoffset_height
FEATURE [PartDesign::Body] Body004  label="BumpSlideStandOff"
  Group = -> [Sketch021,Pad005]
  Origin = -> Origin009
  Placement = pos=(33,3,-6) rot=(0,0,1;0rad)
  Tip = -> Pad005
FEATURE [Sketcher::SketchObject] Sketch022
  FullyConstrained = true
  MapMode = 5
  Support = -> [XY_Plane017]
  expr: Constraints[2] = <<params>>.m25_hole_clear_diam
  expr: Constraints[3] = <<params>>.pinoffset_diam
  sketch-geometry (2):
    g0: Circle CenterX=0 CenterY=0 CenterZ=0 NormalX=0 NormalY=0 NormalZ=1 AngleXU=0 Radius=3
    g1: Circle CenterX=0 CenterY=0 CenterZ=0 NormalX=0 NormalY=0 NormalZ=1 AngleXU=0 Radius=1.4
  constraints (4):
    c: Coincident(g0,g-1)
    c: Coincident(g1,g0)
    c: Diameter(g1) = 2.8
    c: Diameter(g0) = 6
FEATURE [PartDesign::Pad] Pad006  label="MainStandOffExt001"
  Direction = (1,1,1)
  Length = 5
  Length2 = 100
  Profile = -> Sketch022
  Reversed = true
  Type = 0
  expr: Length = <<params>>.pinoffset_height
FEATURE [PartDesign::Body] Body012  label="BumpSlideStandOff001"
  Group = -> [Sketch022,Pad006]
  Origin = -> Origin017
  Placement = pos=(-33,4,-6) rot=(0,0,1;0rad)
  Tip = -> Pad006
FEATURE [App::Part] Part004  label="BumperSlideStandOff_Part"
  Group = -> [Body004,Body012]
  Origin = -> Origin008
  Placement = pos=(0,-3,1) rot=(0,0,1;0rad)
FEATURE [Mesh::Feature] Mesh005  label="BumpMtPlate (Meshed)"
FEATURE [Mesh::Feature] Mesh006  label="BumpWhisker (Meshed)"
FEATURE [Mesh::Feature] Mesh007  label="BumpPivot (Meshed)"
FEATURE [Mesh::Feature] Mesh008  label="BumpSlide (Meshed)"
FEATURE [Mesh::Feature] Mesh009  label="BumpSlidePin (Meshed)"
FEATURE [Mesh::Feature] Mesh010  label="BumpSlideStandOff (Meshed)"
FEATURE [Mesh::Feature] Mesh  label="BumpWhisker (Meshed)001"
